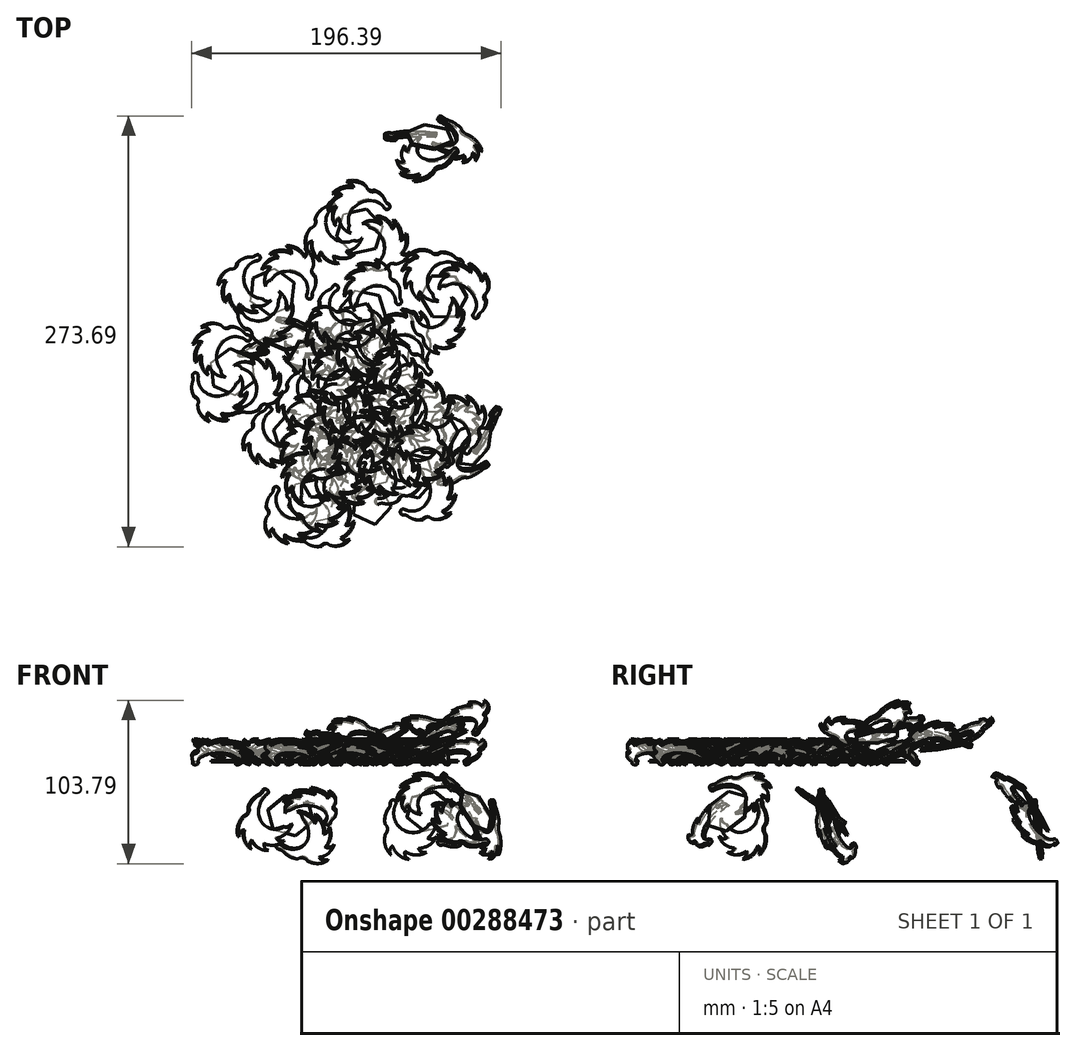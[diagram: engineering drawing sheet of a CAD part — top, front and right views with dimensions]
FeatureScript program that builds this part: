
annotation { "Feature Type Name" : "Feature", "Feature Type Description" : "" }
export const myFeature = defineFeature(function(context is Context, id is Id, definition is map)
    precondition{}
    {
        {
            var Q0;
            Q0=qCreatedBy(makeId("Top.planeOp"),FACE);
            var sketch = newSketch(context, id + "F0", { "sketchPlane" : qUnion([Q0])});
            skCircle(sketch, "E0.cCircle", {"center": v(0, 0) * mm, "radius": 10.32 * mm, "construction": true});
            skLineSegment(sketch, "E0.0", {"start": v(7.5, -10.32) * mm, "end": v(-7.5, -10.32) * mm});
            skLineSegment(sketch, "E0.1", {"start": v(-7.5, -10.32) * mm, "end": v(-12.14, 3.94) * mm});
            skLineSegment(sketch, "E0.2", {"start": v(-12.14, 3.94) * mm, "end": v(0, 12.76) * mm});
            skLineSegment(sketch, "E0.3", {"start": v(0, 12.76) * mm, "end": v(12.14, 3.94) * mm});
            skLineSegment(sketch, "E0.4", {"start": v(12.14, 3.94) * mm, "end": v(7.5, -10.32) * mm});
            skPoint(sketch, "E0.0.midPoint", {"position": v(0, -10.32) * mm});
            skLineSegment(sketch, "E1", {"start": v(0, 12.76) * mm, "end": v(0, -10.32) * mm});
            skSolve(sketch);
        }
        {
            var Q0;
            Q0=qCreatedBy(makeId("Top.planeOp"),FACE);
            var sketch = newSketch(context, id + "F1", { "sketchPlane" : qUnion([Q0])});
            skCircle(sketch, "E2.cCircle", {"center": v(22.17, -7.2) * mm, "radius": 13 * mm, "construction": true});
            skLineSegment(sketch, "E2.0", {"start": v(36.84, -4.09) * mm, "end": v(32.2, -18.35) * mm});
            skLineSegment(sketch, "E2.1", {"start": v(32.2, -18.35) * mm, "end": v(17.54, -21.47) * mm});
            skLineSegment(sketch, "E2.2", {"start": v(17.54, -21.47) * mm, "end": v(7.5, -10.32) * mm});
            skLineSegment(sketch, "E2.3", {"start": v(7.5, -10.32) * mm, "end": v(12.14, 3.94) * mm});
            skLineSegment(sketch, "E2.4", {"start": v(12.14, 3.94) * mm, "end": v(26.8, 7.06) * mm});
            skLineSegment(sketch, "E2.5", {"start": v(26.8, 7.06) * mm, "end": v(36.84, -4.09) * mm});
            skPoint(sketch, "E2.0.midPoint", {"position": v(34.53, -11.22) * mm});
            skSolve(sketch);
        }
        {
            var Q0;
            Q0=makeQuery(id+"F0.imprint","IMPRINT",FACE,{"disambiguationData":[TD([[makeQuery(id+"F0.imprint","IMPRINT",EDGE,{"derivedFrom":sQuery(id+"F0.wireOp",EDGE,"E0.0")}),-1.0]])]});
            extrude(context, id + "F2", {"entities" : qUnion([Q0]), "oppositeDirection" : true, "depth" : 1 * mm});
        }
        {
            var Q0;
            Q0=makeQuery(id+"F1.imprint","IMPRINT",FACE,{"disambiguationData":[TD([[makeQuery(id+"F1.imprint","IMPRINT",EDGE,{"derivedFrom":sQuery(id+"F1.wireOp",EDGE,"E2.0")}),-1.0]])]});
            extrude(context, id + "F3", {"entities" : qUnion([Q0]), "oppositeDirection" : true, "depth" : 1 * mm});
        }
        {
            var Q0;
            Q0=qCreatedBy(makeId("Right.planeOp"),FACE);
            var sketch = newSketch(context, id + "F4", { "sketchPlane" : qUnion([Q0])});
            skLineSegment(sketch, "E3", {"start": v(0, 0) * mm, "end": v(0, 7.73) * mm});
            skSolve(sketch);
        }
        {
            var Q0;
            Q0=makeQuery(id+"F3.opExtrude","SWEPT_BODY",BODY,{"disambiguationData":[OSD([sQuery(id+"F1.wireOp",EDGE,"E2.0"),sQuery(id+"F1.wireOp",EDGE,"E2.1"),sQuery(id+"F1.wireOp",EDGE,"E2.2"),sQuery(id+"F1.wireOp",EDGE,"E2.3"),sQuery(id+"F1.wireOp",EDGE,"E2.4"),sQuery(id+"F1.wireOp",EDGE,"E2.5")])]});
            var Q1;
            Q1=sQuery(id+"F4.wireOp",EDGE,"E3");
            circularPattern(context, id + "F5", {"entities" : qUnion([Q0]), "axis" : qUnion([Q1]), "angle" : 72 * degree, "instanceCount" : round(5)});
        }
        {
            var Q0;
            Q0=makeQuery(id+"F5.opPattern","COPY",FACE,{"derivedFrom":makeQuery(id+"F3.opExtrude","CAP_FACE",FACE,{"disambiguationData":[OSD([sQuery(id+"F1.wireOp",EDGE,"E2.0"),sQuery(id+"F1.wireOp",EDGE,"E2.1"),sQuery(id+"F1.wireOp",EDGE,"E2.2"),sQuery(id+"F1.wireOp",EDGE,"E2.3"),sQuery(id+"F1.wireOp",EDGE,"E2.4"),sQuery(id+"F1.wireOp",EDGE,"E2.5")])],"isStart":true}),"instanceName":"4"});
            var sketch = newSketch(context, id + "F6", { "sketchPlane" : qUnion([Q0])});
            skLineSegment(sketch, "E4", {"start": v(0, -36.3) * mm, "end": v(0, -10.32) * mm});
            skLineSegment(sketch, "E5", {"start": v(-15, -23.31) * mm, "end": v(15, -23.31) * mm});
            skCircle(sketch, "E6", {"center": v(0, -23.31) * mm, "radius": 3.24 * mm});
            skSolve(sketch);
        }
        {
            var Q0;
            Q0=qCreatedBy(makeId("Right.planeOp"),FACE);
            var sketch = newSketch(context, id + "F7", { "sketchPlane" : qUnion([Q0])});
            skArc(sketch, "E7.0", {"start": v(-1.37, 0) * mm, "mid": v(-13.44, 15.63) * mm, "end": v(-25.5, 0) * mm});
            skLineSegment(sketch, "E8", {"start": v(-25.27, 0) * mm, "end": v(-25.5, 0) * mm});
            skLineSegment(sketch, "E9", {"start": v(-1.37, 0) * mm, "end": v(0, 0) * mm});
            skArc(sketch, "E10", {"start": v(1.07, 1.27) * mm, "mid": v(3.46, 7.37) * mm, "end": v(2.5, 13.85) * mm});
            skArc(sketch, "E11", {"start": v(0.8, 19.96) * mm, "mid": v(0.27, 16.52) * mm, "end": v(2.5, 13.85) * mm});
            skArc(sketch, "E12.1.0", {"start": v(0.8, 19.96) * mm, "mid": v(-0.54, 26.93) * mm, "end": v(-5.4, 32.1) * mm});
            skArc(sketch, "E12.1.1", {"start": v(-5.16, 26.31) * mm, "mid": v(-4.13, 29.25) * mm, "end": v(-5.4, 32.1) * mm});
            skArc(sketch, "E12.2.0", {"start": v(-5.16, 26.31) * mm, "mid": v(-10.33, 31.17) * mm, "end": v(-17.3, 32.5) * mm});
            skArc(sketch, "E12.2.1", {"start": v(-13.71, 27.95) * mm, "mid": v(-14.6, 30.93) * mm, "end": v(-17.3, 32.5) * mm});
            skArc(sketch, "E12.3.0", {"start": v(-13.71, 27.95) * mm, "mid": v(-20.75, 28.84) * mm, "end": v(-27.16, 25.82) * mm});
            skArc(sketch, "E12.3.1", {"start": v(-21.6, 24.25) * mm, "mid": v(-24.07, 26.14) * mm, "end": v(-27.16, 25.82) * mm});
            skArc(sketch, "E12.4.0", {"start": v(-21.6, 24.25) * mm, "mid": v(-27.8, 20.83) * mm, "end": v(-31.22, 14.62) * mm});
            skArc(sketch, "E12.4.1", {"start": v(-25.8, 16.63) * mm, "mid": v(-28.9, 16.7) * mm, "end": v(-31.22, 14.62) * mm});
            skArc(sketch, "E12.5.0", {"start": v(-25.8, 16.63) * mm, "mid": v(-28.8, 10.21) * mm, "end": v(-27.92, 3.18) * mm});
            skArc(sketch, "E12.5.1", {"start": v(-24.7, 7.99) * mm, "mid": v(-27.27, 6.22) * mm, "end": v(-27.92, 3.18) * mm});
            skArc(sketch, "E12.6.0", {"start": v(-24.7, 7.99) * mm, "mid": v(-25.75, 4.06) * mm, "end": v(-25.5, 0) * mm});
            skLineSegment(sketch, "E13", {"start": v(-25.5, 0) * mm, "end": v(-25.5, 0) * mm});
            skArc(sketch, "E14", {"start": v(-1.37, 0) * mm, "mid": v(1.27, -2.11) * mm, "end": v(1.07, 1.27) * mm});
            skSolve(sketch);
        }
        {
            var Q0;
            {var subQ2=sQuery(id+"F7.wireOp",EDGE,"E7.0");Q0=makeQuery(id+"F7.imprint","IMPRINT",FACE,{"disambiguationData":[TD([[makeQuery(id+"F7.imprint","IMPRINT",EDGE,{"derivedFrom":subQ2}),-1.0]])]});}
            extrude(context, id + "F8", {"entities" : qUnion([Q0]), "oppositeDirection" : true, "depth" : 2 * mm});
        }
        {
            var Q0;
            Q0=makeQuery(id+"F8.opExtrude","SWEPT_EDGE",EDGE,{"disambiguationData":[OSD([sQuery(id+"F7.wireOp",EDGE,"E10"),sQuery(id+"F7.wireOp",EDGE,"E14")])]});
            fillet(context, id + "F9", {"entities" : qUnion([Q0]), "radius" : 5 * mm, "tangentPropagation" : true, "allowEdgeOverflow" : false});
        }
        {
            var Q0;
            Q0=qCreatedBy(makeId("Right.planeOp"),FACE);
            var sketch = newSketch(context, id + "F10", { "sketchPlane" : qUnion([Q0])});
            skLineSegment(sketch, "E15", {"start": v(0, 0) * mm, "end": v(-23.31, 0) * mm});
            skLineSegment(sketch, "E16", {"start": v(0, 0) * mm, "end": v(0, 28.42) * mm});
            skSolve(sketch);
        }
        {
            var Q0;
            Q0=makeQuery(id+"F8.opExtrude","SWEPT_BODY",BODY,{"disambiguationData":[OSD([sQuery(id+"F7.wireOp",EDGE,"003f2e54-bd62-4f0b-a98e-8c36e71e2cf6"),sQuery(id+"F7.wireOp",EDGE,"8c729305-40a1-49fa-b790-4b99a3909bb6"),sQuery(id+"F7.wireOp",EDGE,"862a2a8f-3db7-4421-9c69-6ab2f53c4c24.1.0"),sQuery(id+"F7.wireOp",EDGE,"862a2a8f-3db7-4421-9c69-6ab2f53c4c24.1.1"),sQuery(id+"F7.wireOp",EDGE,"862a2a8f-3db7-4421-9c69-6ab2f53c4c24.2.0"),sQuery(id+"F7.wireOp",EDGE,"862a2a8f-3db7-4421-9c69-6ab2f53c4c24.2.1"),sQuery(id+"F7.wireOp",EDGE,"862a2a8f-3db7-4421-9c69-6ab2f53c4c24.3.0"),sQuery(id+"F7.wireOp",EDGE,"862a2a8f-3db7-4421-9c69-6ab2f53c4c24.3.1"),sQuery(id+"F7.wireOp",EDGE,"862a2a8f-3db7-4421-9c69-6ab2f53c4c24.4.0"),sQuery(id+"F7.wireOp",EDGE,"862a2a8f-3db7-4421-9c69-6ab2f53c4c24.4.1"),sQuery(id+"F7.wireOp",EDGE,"862a2a8f-3db7-4421-9c69-6ab2f53c4c24.5.0"),sQuery(id+"F7.wireOp",EDGE,"E7.0"),sQuery(id+"F7.wireOp",EDGE,"E8"),sQuery(id+"F7.wireOp",EDGE,"E9")])]});
            var Q1;
            Q1=sQuery(id+"F10.wireOp",EDGE,"E15");
            transform(context, id + "F11", {"entities" : qUnion([Q0]), "transformType" : TransformType.ROTATION, "transformAxis" : qUnion([Q1]), "angle" : 65 * degree, "makeCopy" : false});
        }
        {
            var Q0;
            Q0=makeQuery(id+"F8.opExtrude","SWEPT_BODY",BODY,{"disambiguationData":[OSD([sQuery(id+"F7.wireOp",EDGE,"003f2e54-bd62-4f0b-a98e-8c36e71e2cf6"),sQuery(id+"F7.wireOp",EDGE,"8c729305-40a1-49fa-b790-4b99a3909bb6"),sQuery(id+"F7.wireOp",EDGE,"862a2a8f-3db7-4421-9c69-6ab2f53c4c24.1.0"),sQuery(id+"F7.wireOp",EDGE,"862a2a8f-3db7-4421-9c69-6ab2f53c4c24.1.1"),sQuery(id+"F7.wireOp",EDGE,"862a2a8f-3db7-4421-9c69-6ab2f53c4c24.2.0"),sQuery(id+"F7.wireOp",EDGE,"862a2a8f-3db7-4421-9c69-6ab2f53c4c24.2.1"),sQuery(id+"F7.wireOp",EDGE,"862a2a8f-3db7-4421-9c69-6ab2f53c4c24.3.0"),sQuery(id+"F7.wireOp",EDGE,"862a2a8f-3db7-4421-9c69-6ab2f53c4c24.3.1"),sQuery(id+"F7.wireOp",EDGE,"862a2a8f-3db7-4421-9c69-6ab2f53c4c24.4.0"),sQuery(id+"F7.wireOp",EDGE,"862a2a8f-3db7-4421-9c69-6ab2f53c4c24.4.1"),sQuery(id+"F7.wireOp",EDGE,"862a2a8f-3db7-4421-9c69-6ab2f53c4c24.5.0"),sQuery(id+"F7.wireOp",EDGE,"E7.0"),sQuery(id+"F7.wireOp",EDGE,"E8"),sQuery(id+"F7.wireOp",EDGE,"E9")])]});
            var Q1;
            Q1=sQuery(id+"F10.wireOp",EDGE,"E16");
            circularPattern(context, id + "F12", {"entities" : qUnion([Q0]), "axis" : qUnion([Q1]), "angle" : 72 * degree, "instanceCount" : round(5)});
        }
        {
            var Q0;
            Q0=qCreatedBy(makeId("Right.planeOp"),FACE);
            var sketch = newSketch(context, id + "F13", { "sketchPlane" : qUnion([Q0])});
            skLineSegment(sketch, "E17.0", {"start": v(-36.3, 0) * mm, "end": v(-10.32, 0) * mm});
            skLineSegment(sketch, "E18", {"start": v(-23.31, 0) * mm, "end": v(-23.31, 15.48) * mm});
            skSolve(sketch);
        }
        {
            var Q0;
            Q0=makeQuery(id+"F8.opExtrude","SWEPT_BODY",BODY,{"disambiguationData":[OSD([sQuery(id+"F7.wireOp",EDGE,"003f2e54-bd62-4f0b-a98e-8c36e71e2cf6"),sQuery(id+"F7.wireOp",EDGE,"8c729305-40a1-49fa-b790-4b99a3909bb6"),sQuery(id+"F7.wireOp",EDGE,"862a2a8f-3db7-4421-9c69-6ab2f53c4c24.1.0"),sQuery(id+"F7.wireOp",EDGE,"862a2a8f-3db7-4421-9c69-6ab2f53c4c24.1.1"),sQuery(id+"F7.wireOp",EDGE,"862a2a8f-3db7-4421-9c69-6ab2f53c4c24.2.0"),sQuery(id+"F7.wireOp",EDGE,"862a2a8f-3db7-4421-9c69-6ab2f53c4c24.2.1"),sQuery(id+"F7.wireOp",EDGE,"862a2a8f-3db7-4421-9c69-6ab2f53c4c24.3.0"),sQuery(id+"F7.wireOp",EDGE,"862a2a8f-3db7-4421-9c69-6ab2f53c4c24.3.1"),sQuery(id+"F7.wireOp",EDGE,"862a2a8f-3db7-4421-9c69-6ab2f53c4c24.4.0"),sQuery(id+"F7.wireOp",EDGE,"862a2a8f-3db7-4421-9c69-6ab2f53c4c24.4.1"),sQuery(id+"F7.wireOp",EDGE,"862a2a8f-3db7-4421-9c69-6ab2f53c4c24.5.0"),sQuery(id+"F7.wireOp",EDGE,"E7.0"),sQuery(id+"F7.wireOp",EDGE,"E8"),sQuery(id+"F7.wireOp",EDGE,"E9")])]});
            var Q1;
            Q1=sQuery(id+"F13.wireOp",EDGE,"E18");
            circularPattern(context, id + "F14", {"entities" : qUnion([Q0]), "axis" : qUnion([Q1]), "angle" : 120 * degree, "instanceCount" : round(3)});
        }
        {
            var Q0;
            Q0=makeQuery(id+"F14.opPattern","COPY",BODY,{"derivedFrom":makeQuery(id+"F8.opExtrude","SWEPT_BODY",BODY,{"disambiguationData":[OSD([sQuery(id+"F7.wireOp",EDGE,"E7.0"),sQuery(id+"F7.wireOp",EDGE,"E10"),sQuery(id+"F7.wireOp",EDGE,"E11"),sQuery(id+"F7.wireOp",EDGE,"E12.1.0"),sQuery(id+"F7.wireOp",EDGE,"E12.1.1"),sQuery(id+"F7.wireOp",EDGE,"E12.2.0"),sQuery(id+"F7.wireOp",EDGE,"E12.2.1"),sQuery(id+"F7.wireOp",EDGE,"E12.3.0"),sQuery(id+"F7.wireOp",EDGE,"E12.3.1"),sQuery(id+"F7.wireOp",EDGE,"E12.4.0"),sQuery(id+"F7.wireOp",EDGE,"E12.4.1"),sQuery(id+"F7.wireOp",EDGE,"E12.5.0"),sQuery(id+"F7.wireOp",EDGE,"E12.5.1"),sQuery(id+"F7.wireOp",EDGE,"E12.6.0"),sQuery(id+"F7.wireOp",EDGE,"E13"),sQuery(id+"F7.wireOp",EDGE,"E14")])]}),"instanceName":"2"});
            var Q1;
            Q1=makeQuery(id+"F14.opPattern","COPY",BODY,{"derivedFrom":makeQuery(id+"F8.opExtrude","SWEPT_BODY",BODY,{"disambiguationData":[OSD([sQuery(id+"F7.wireOp",EDGE,"E7.0"),sQuery(id+"F7.wireOp",EDGE,"E10"),sQuery(id+"F7.wireOp",EDGE,"E11"),sQuery(id+"F7.wireOp",EDGE,"E12.1.0"),sQuery(id+"F7.wireOp",EDGE,"E12.1.1"),sQuery(id+"F7.wireOp",EDGE,"E12.2.0"),sQuery(id+"F7.wireOp",EDGE,"E12.2.1"),sQuery(id+"F7.wireOp",EDGE,"E12.3.0"),sQuery(id+"F7.wireOp",EDGE,"E12.3.1"),sQuery(id+"F7.wireOp",EDGE,"E12.4.0"),sQuery(id+"F7.wireOp",EDGE,"E12.4.1"),sQuery(id+"F7.wireOp",EDGE,"E12.5.0"),sQuery(id+"F7.wireOp",EDGE,"E12.5.1"),sQuery(id+"F7.wireOp",EDGE,"E12.6.0"),sQuery(id+"F7.wireOp",EDGE,"E13"),sQuery(id+"F7.wireOp",EDGE,"E14")])]}),"instanceName":"1"});
            var Q2;
            Q2=sQuery(id+"F10.wireOp",EDGE,"E16");
            circularPattern(context, id + "F15", {"entities" : qUnion([Q0, Q1]), "axis" : qUnion([Q2]), "angle" : 72 * degree, "instanceCount" : round(5)});
        }
        {
            var Q0;
            Q0=makeQuery(id+"F3.opExtrude","SWEPT_BODY",BODY,{"disambiguationData":[OSD([sQuery(id+"F1.wireOp",EDGE,"E2.0"),sQuery(id+"F1.wireOp",EDGE,"E2.1"),sQuery(id+"F1.wireOp",EDGE,"E2.2"),sQuery(id+"F1.wireOp",EDGE,"E2.3"),sQuery(id+"F1.wireOp",EDGE,"E2.4"),sQuery(id+"F1.wireOp",EDGE,"E2.5")])]});
            var Q1;
            Q1=makeQuery(id+"F15.opPattern","COPY",BODY,{"derivedFrom":makeQuery(id+"F14.opPattern","COPY",BODY,{"derivedFrom":makeQuery(id+"F8.opExtrude","SWEPT_BODY",BODY,{"disambiguationData":[OSD([sQuery(id+"F7.wireOp",EDGE,"E7.0"),sQuery(id+"F7.wireOp",EDGE,"E10"),sQuery(id+"F7.wireOp",EDGE,"E11"),sQuery(id+"F7.wireOp",EDGE,"E12.1.0"),sQuery(id+"F7.wireOp",EDGE,"E12.1.1"),sQuery(id+"F7.wireOp",EDGE,"E12.2.0"),sQuery(id+"F7.wireOp",EDGE,"E12.2.1"),sQuery(id+"F7.wireOp",EDGE,"E12.3.0"),sQuery(id+"F7.wireOp",EDGE,"E12.3.1"),sQuery(id+"F7.wireOp",EDGE,"E12.4.0"),sQuery(id+"F7.wireOp",EDGE,"E12.4.1"),sQuery(id+"F7.wireOp",EDGE,"E12.5.0"),sQuery(id+"F7.wireOp",EDGE,"E12.5.1"),sQuery(id+"F7.wireOp",EDGE,"E12.6.0"),sQuery(id+"F7.wireOp",EDGE,"E13"),sQuery(id+"F7.wireOp",EDGE,"E14")])]}),"instanceName":"1"}),"instanceName":"1"});
            var Q2;
            Q2=makeQuery(id+"F12.opPattern","COPY",BODY,{"derivedFrom":makeQuery(id+"F8.opExtrude","SWEPT_BODY",BODY,{"disambiguationData":[OSD([sQuery(id+"F7.wireOp",EDGE,"E7.0"),sQuery(id+"F7.wireOp",EDGE,"E10"),sQuery(id+"F7.wireOp",EDGE,"E11"),sQuery(id+"F7.wireOp",EDGE,"E12.1.0"),sQuery(id+"F7.wireOp",EDGE,"E12.1.1"),sQuery(id+"F7.wireOp",EDGE,"E12.2.0"),sQuery(id+"F7.wireOp",EDGE,"E12.2.1"),sQuery(id+"F7.wireOp",EDGE,"E12.3.0"),sQuery(id+"F7.wireOp",EDGE,"E12.3.1"),sQuery(id+"F7.wireOp",EDGE,"E12.4.0"),sQuery(id+"F7.wireOp",EDGE,"E12.4.1"),sQuery(id+"F7.wireOp",EDGE,"E12.5.0"),sQuery(id+"F7.wireOp",EDGE,"E12.5.1"),sQuery(id+"F7.wireOp",EDGE,"E12.6.0"),sQuery(id+"F7.wireOp",EDGE,"E13"),sQuery(id+"F7.wireOp",EDGE,"E14")])]}),"instanceName":"1"});
            var Q3;
            Q3=makeQuery(id+"F15.opPattern","COPY",BODY,{"derivedFrom":makeQuery(id+"F14.opPattern","COPY",BODY,{"derivedFrom":makeQuery(id+"F8.opExtrude","SWEPT_BODY",BODY,{"disambiguationData":[OSD([sQuery(id+"F7.wireOp",EDGE,"E7.0"),sQuery(id+"F7.wireOp",EDGE,"E10"),sQuery(id+"F7.wireOp",EDGE,"E11"),sQuery(id+"F7.wireOp",EDGE,"E12.1.0"),sQuery(id+"F7.wireOp",EDGE,"E12.1.1"),sQuery(id+"F7.wireOp",EDGE,"E12.2.0"),sQuery(id+"F7.wireOp",EDGE,"E12.2.1"),sQuery(id+"F7.wireOp",EDGE,"E12.3.0"),sQuery(id+"F7.wireOp",EDGE,"E12.3.1"),sQuery(id+"F7.wireOp",EDGE,"E12.4.0"),sQuery(id+"F7.wireOp",EDGE,"E12.4.1"),sQuery(id+"F7.wireOp",EDGE,"E12.5.0"),sQuery(id+"F7.wireOp",EDGE,"E12.5.1"),sQuery(id+"F7.wireOp",EDGE,"E12.6.0"),sQuery(id+"F7.wireOp",EDGE,"E13"),sQuery(id+"F7.wireOp",EDGE,"E14")])]}),"instanceName":"2"}),"instanceName":"1"});
            var Q4;
            Q4=sQuery(id+"F13.wireOp",EDGE,"E18");
            circularPattern(context, id + "F16", {"entities" : qUnion([Q0, Q1, Q2, Q3]), "axis" : qUnion([Q4]), "angle" : 120 * degree, "instanceCount" : 2, "oppositeDirection" : true});
        }
        {
            var Q0;
            Q0=makeQuery(id+"F2.opExtrude","SWEPT_BODY",BODY,{"disambiguationData":[OSD([sQuery(id+"F0.wireOp",EDGE,"E0.0"),sQuery(id+"F0.wireOp",EDGE,"E0.1"),sQuery(id+"F0.wireOp",EDGE,"E0.2"),sQuery(id+"F0.wireOp",EDGE,"E0.3"),sQuery(id+"F0.wireOp",EDGE,"E0.4")])]});
            var Q1;
            Q1=makeQuery(id+"F12.opPattern","COPY",BODY,{"derivedFrom":makeQuery(id+"F8.opExtrude","SWEPT_BODY",BODY,{"disambiguationData":[OSD([sQuery(id+"F7.wireOp",EDGE,"E7.0"),sQuery(id+"F7.wireOp",EDGE,"E10"),sQuery(id+"F7.wireOp",EDGE,"E11"),sQuery(id+"F7.wireOp",EDGE,"E12.1.0"),sQuery(id+"F7.wireOp",EDGE,"E12.1.1"),sQuery(id+"F7.wireOp",EDGE,"E12.2.0"),sQuery(id+"F7.wireOp",EDGE,"E12.2.1"),sQuery(id+"F7.wireOp",EDGE,"E12.3.0"),sQuery(id+"F7.wireOp",EDGE,"E12.3.1"),sQuery(id+"F7.wireOp",EDGE,"E12.4.0"),sQuery(id+"F7.wireOp",EDGE,"E12.4.1"),sQuery(id+"F7.wireOp",EDGE,"E12.5.0"),sQuery(id+"F7.wireOp",EDGE,"E12.5.1"),sQuery(id+"F7.wireOp",EDGE,"E12.6.0"),sQuery(id+"F7.wireOp",EDGE,"E13"),sQuery(id+"F7.wireOp",EDGE,"E14")])]}),"instanceName":"2"});
            var Q2;
            Q2=makeQuery(id+"F12.opPattern","COPY",BODY,{"derivedFrom":makeQuery(id+"F8.opExtrude","SWEPT_BODY",BODY,{"disambiguationData":[OSD([sQuery(id+"F7.wireOp",EDGE,"E7.0"),sQuery(id+"F7.wireOp",EDGE,"E10"),sQuery(id+"F7.wireOp",EDGE,"E11"),sQuery(id+"F7.wireOp",EDGE,"E12.1.0"),sQuery(id+"F7.wireOp",EDGE,"E12.1.1"),sQuery(id+"F7.wireOp",EDGE,"E12.2.0"),sQuery(id+"F7.wireOp",EDGE,"E12.2.1"),sQuery(id+"F7.wireOp",EDGE,"E12.3.0"),sQuery(id+"F7.wireOp",EDGE,"E12.3.1"),sQuery(id+"F7.wireOp",EDGE,"E12.4.0"),sQuery(id+"F7.wireOp",EDGE,"E12.4.1"),sQuery(id+"F7.wireOp",EDGE,"E12.5.0"),sQuery(id+"F7.wireOp",EDGE,"E12.5.1"),sQuery(id+"F7.wireOp",EDGE,"E12.6.0"),sQuery(id+"F7.wireOp",EDGE,"E13"),sQuery(id+"F7.wireOp",EDGE,"E14")])]}),"instanceName":"3"});
            var Q3;
            Q3=sQuery(id+"F13.wireOp",EDGE,"E18");
            circularPattern(context, id + "F17", {"entities" : qUnion([Q0, Q1, Q2]), "axis" : qUnion([Q3]), "angle" : 120 * degree, "instanceCount" : round(3)});
        }
        {
            var Q0;
            Q0=makeQuery(id+"F17.opPattern","COPY",FACE,{"derivedFrom":makeQuery(id+"F2.opExtrude","CAP_FACE",FACE,{"disambiguationData":[OSD([sQuery(id+"F0.wireOp",EDGE,"E0.0"),sQuery(id+"F0.wireOp",EDGE,"E0.1"),sQuery(id+"F0.wireOp",EDGE,"E0.2"),sQuery(id+"F0.wireOp",EDGE,"E0.3"),sQuery(id+"F0.wireOp",EDGE,"E0.4")])],"isStart":true}),"instanceName":"1"});
            var sketch = newSketch(context, id + "F18", { "sketchPlane" : qUnion([Q0])});
            skLineSegment(sketch, "E19", {"start": v(-11.25, -29.8) * mm, "end": v(-31.24, -41.35) * mm});
            skLineSegment(sketch, "E20", {"start": v(-19.97, -22.2) * mm, "end": v(-12.52, -41.88) * mm});
            skSolve(sketch);
        }
        {
            var Q0;
            Q0=sQuery(id+"F18.wireOp",VERTEX,"E19.end");
            var Q1;
            Q1=sQuery(id+"F18.wireOp",VERTEX,"E19.start");
            var Q2;
            Q2=sQuery(id+"F13.wireOp",VERTEX,"E18.end");
            cPlane(context, id + "F19", {"entities" : qUnion([Q0, Q1, Q2]), "cplaneType" : CPlaneType.THREE_POINT, "offset" : 150 * mm, "width" : 150 * mm, "height" : 150 * mm});
        }
        {
            var Q0;
            Q0=qCreatedBy(id+"F19.planeOp",FACE);
            var sketch = newSketch(context, id + "F20", { "sketchPlane" : qUnion([Q0])});
            skLineSegment(sketch, "E21.0", {"start": v(24.65, 0) * mm, "end": v(47.73, 0) * mm});
            skLineSegment(sketch, "E21.1", {"start": v(28.4, 0) * mm, "end": v(31.78, 0) * mm});
            skLineSegment(sketch, "E22", {"start": v(31.8, 0) * mm, "end": v(31.8, 2.35) * mm});
            skLineSegment(sketch, "E23", {"start": v(31.8, 2.35) * mm, "end": v(31.8, 9.54) * mm});
            skSolve(sketch);
        }
        {
            var Q0;
            Q0=makeQuery(id+"F16.opPattern","COPY",BODY,{"derivedFrom":makeQuery(id+"F3.opExtrude","SWEPT_BODY",BODY,{"disambiguationData":[OSD([sQuery(id+"F1.wireOp",EDGE,"E2.0"),sQuery(id+"F1.wireOp",EDGE,"E2.1"),sQuery(id+"F1.wireOp",EDGE,"E2.2"),sQuery(id+"F1.wireOp",EDGE,"E2.3"),sQuery(id+"F1.wireOp",EDGE,"E2.4"),sQuery(id+"F1.wireOp",EDGE,"E2.5")])]}),"instanceName":"1"});
            var Q1;
            Q1=makeQuery(id+"F16.opPattern","COPY",BODY,{"derivedFrom":makeQuery(id+"F12.opPattern","COPY",BODY,{"derivedFrom":makeQuery(id+"F8.opExtrude","SWEPT_BODY",BODY,{"disambiguationData":[OSD([sQuery(id+"F7.wireOp",EDGE,"E7.0"),sQuery(id+"F7.wireOp",EDGE,"E10"),sQuery(id+"F7.wireOp",EDGE,"E11"),sQuery(id+"F7.wireOp",EDGE,"E12.1.0"),sQuery(id+"F7.wireOp",EDGE,"E12.1.1"),sQuery(id+"F7.wireOp",EDGE,"E12.2.0"),sQuery(id+"F7.wireOp",EDGE,"E12.2.1"),sQuery(id+"F7.wireOp",EDGE,"E12.3.0"),sQuery(id+"F7.wireOp",EDGE,"E12.3.1"),sQuery(id+"F7.wireOp",EDGE,"E12.4.0"),sQuery(id+"F7.wireOp",EDGE,"E12.4.1"),sQuery(id+"F7.wireOp",EDGE,"E12.5.0"),sQuery(id+"F7.wireOp",EDGE,"E12.5.1"),sQuery(id+"F7.wireOp",EDGE,"E12.6.0"),sQuery(id+"F7.wireOp",EDGE,"E13"),sQuery(id+"F7.wireOp",EDGE,"E14")])]}),"instanceName":"1"}),"instanceName":"1"});
            var Q2;
            Q2=makeQuery(id+"F16.opPattern","COPY",BODY,{"derivedFrom":makeQuery(id+"F15.opPattern","COPY",BODY,{"derivedFrom":makeQuery(id+"F14.opPattern","COPY",BODY,{"derivedFrom":makeQuery(id+"F8.opExtrude","SWEPT_BODY",BODY,{"disambiguationData":[OSD([sQuery(id+"F7.wireOp",EDGE,"E7.0"),sQuery(id+"F7.wireOp",EDGE,"E10"),sQuery(id+"F7.wireOp",EDGE,"E11"),sQuery(id+"F7.wireOp",EDGE,"E12.1.0"),sQuery(id+"F7.wireOp",EDGE,"E12.1.1"),sQuery(id+"F7.wireOp",EDGE,"E12.2.0"),sQuery(id+"F7.wireOp",EDGE,"E12.2.1"),sQuery(id+"F7.wireOp",EDGE,"E12.3.0"),sQuery(id+"F7.wireOp",EDGE,"E12.3.1"),sQuery(id+"F7.wireOp",EDGE,"E12.4.0"),sQuery(id+"F7.wireOp",EDGE,"E12.4.1"),sQuery(id+"F7.wireOp",EDGE,"E12.5.0"),sQuery(id+"F7.wireOp",EDGE,"E12.5.1"),sQuery(id+"F7.wireOp",EDGE,"E12.6.0"),sQuery(id+"F7.wireOp",EDGE,"E13"),sQuery(id+"F7.wireOp",EDGE,"E14")])]}),"instanceName":"2"}),"instanceName":"1"}),"instanceName":"1"});
            var Q3;
            Q3=makeQuery(id+"F16.opPattern","COPY",BODY,{"derivedFrom":makeQuery(id+"F15.opPattern","COPY",BODY,{"derivedFrom":makeQuery(id+"F14.opPattern","COPY",BODY,{"derivedFrom":makeQuery(id+"F8.opExtrude","SWEPT_BODY",BODY,{"disambiguationData":[OSD([sQuery(id+"F7.wireOp",EDGE,"E7.0"),sQuery(id+"F7.wireOp",EDGE,"E10"),sQuery(id+"F7.wireOp",EDGE,"E11"),sQuery(id+"F7.wireOp",EDGE,"E12.1.0"),sQuery(id+"F7.wireOp",EDGE,"E12.1.1"),sQuery(id+"F7.wireOp",EDGE,"E12.2.0"),sQuery(id+"F7.wireOp",EDGE,"E12.2.1"),sQuery(id+"F7.wireOp",EDGE,"E12.3.0"),sQuery(id+"F7.wireOp",EDGE,"E12.3.1"),sQuery(id+"F7.wireOp",EDGE,"E12.4.0"),sQuery(id+"F7.wireOp",EDGE,"E12.4.1"),sQuery(id+"F7.wireOp",EDGE,"E12.5.0"),sQuery(id+"F7.wireOp",EDGE,"E12.5.1"),sQuery(id+"F7.wireOp",EDGE,"E12.6.0"),sQuery(id+"F7.wireOp",EDGE,"E13"),sQuery(id+"F7.wireOp",EDGE,"E14")])]}),"instanceName":"1"}),"instanceName":"1"}),"instanceName":"1"});
            var Q4;
            Q4=sQuery(id+"F20.wireOp",EDGE,"E22");
            circularPattern(context, id + "F21", {"entities" : qUnion([Q0, Q1, Q2, Q3]), "axis" : qUnion([Q4]), "angle" : 72 * degree, "instanceCount" : round(3), "oppositeDirection" : true});
        }
        {
            var Q0;
            Q0=makeQuery(id+"F17.opPattern","COPY",FACE,{"derivedFrom":makeQuery(id+"F2.opExtrude","CAP_FACE",FACE,{"disambiguationData":[OSD([sQuery(id+"F0.wireOp",EDGE,"E0.0"),sQuery(id+"F0.wireOp",EDGE,"E0.1"),sQuery(id+"F0.wireOp",EDGE,"E0.2"),sQuery(id+"F0.wireOp",EDGE,"E0.3"),sQuery(id+"F0.wireOp",EDGE,"E0.4")])],"isStart":true}),"instanceName":"2"});
            var sketch = newSketch(context, id + "F22", { "sketchPlane" : qUnion([Q0])});
            skLineSegment(sketch, "E24", {"start": v(11.25, -29.8) * mm, "end": v(31.24, -41.35) * mm});
            skLineSegment(sketch, "E25", {"start": v(17.54, -47.45) * mm, "end": v(22.34, -24.87) * mm});
            skSolve(sketch);
        }
        {
            var Q0;
            Q0=sQuery(id+"F22.wireOp",VERTEX,"E24.end");
            var Q1;
            Q1=sQuery(id+"F22.wireOp",VERTEX,"E24.start");
            var Q2;
            Q2=sQuery(id+"F13.wireOp",VERTEX,"E18.end");
            cPlane(context, id + "F23", {"entities" : qUnion([Q0, Q1, Q2]), "cplaneType" : CPlaneType.THREE_POINT, "offset" : 150 * mm, "width" : 150 * mm, "height" : 150 * mm});
        }
        {
            var Q0;
            Q0=qCreatedBy(id+"F23.planeOp",FACE);
            var sketch = newSketch(context, id + "F24", { "sketchPlane" : qUnion([Q0])});
            skLineSegment(sketch, "E26.0", {"start": v(24.65, 0) * mm, "end": v(47.73, 0) * mm});
            skLineSegment(sketch, "E26.1", {"start": v(38.91, 0) * mm, "end": v(31.78, 0) * mm});
            skLineSegment(sketch, "E27", {"start": v(31.8, 0) * mm, "end": v(31.8, 7.31) * mm});
            skSolve(sketch);
        }
        {
            var Q0;
            Q0=makeQuery(id+"F3.opExtrude","SWEPT_BODY",BODY,{"disambiguationData":[OSD([sQuery(id+"F1.wireOp",EDGE,"E2.0"),sQuery(id+"F1.wireOp",EDGE,"E2.1"),sQuery(id+"F1.wireOp",EDGE,"E2.2"),sQuery(id+"F1.wireOp",EDGE,"E2.3"),sQuery(id+"F1.wireOp",EDGE,"E2.4"),sQuery(id+"F1.wireOp",EDGE,"E2.5")])]});
            var Q1;
            Q1=makeQuery(id+"F15.opPattern","COPY",BODY,{"derivedFrom":makeQuery(id+"F14.opPattern","COPY",BODY,{"derivedFrom":makeQuery(id+"F8.opExtrude","SWEPT_BODY",BODY,{"disambiguationData":[OSD([sQuery(id+"F7.wireOp",EDGE,"E7.0"),sQuery(id+"F7.wireOp",EDGE,"E10"),sQuery(id+"F7.wireOp",EDGE,"E11"),sQuery(id+"F7.wireOp",EDGE,"E12.1.0"),sQuery(id+"F7.wireOp",EDGE,"E12.1.1"),sQuery(id+"F7.wireOp",EDGE,"E12.2.0"),sQuery(id+"F7.wireOp",EDGE,"E12.2.1"),sQuery(id+"F7.wireOp",EDGE,"E12.3.0"),sQuery(id+"F7.wireOp",EDGE,"E12.3.1"),sQuery(id+"F7.wireOp",EDGE,"E12.4.0"),sQuery(id+"F7.wireOp",EDGE,"E12.4.1"),sQuery(id+"F7.wireOp",EDGE,"E12.5.0"),sQuery(id+"F7.wireOp",EDGE,"E12.5.1"),sQuery(id+"F7.wireOp",EDGE,"E12.6.0"),sQuery(id+"F7.wireOp",EDGE,"E13"),sQuery(id+"F7.wireOp",EDGE,"E14")])]}),"instanceName":"2"}),"instanceName":"1"});
            var Q2;
            Q2=makeQuery(id+"F12.opPattern","COPY",BODY,{"derivedFrom":makeQuery(id+"F8.opExtrude","SWEPT_BODY",BODY,{"disambiguationData":[OSD([sQuery(id+"F7.wireOp",EDGE,"E7.0"),sQuery(id+"F7.wireOp",EDGE,"E10"),sQuery(id+"F7.wireOp",EDGE,"E11"),sQuery(id+"F7.wireOp",EDGE,"E12.1.0"),sQuery(id+"F7.wireOp",EDGE,"E12.1.1"),sQuery(id+"F7.wireOp",EDGE,"E12.2.0"),sQuery(id+"F7.wireOp",EDGE,"E12.2.1"),sQuery(id+"F7.wireOp",EDGE,"E12.3.0"),sQuery(id+"F7.wireOp",EDGE,"E12.3.1"),sQuery(id+"F7.wireOp",EDGE,"E12.4.0"),sQuery(id+"F7.wireOp",EDGE,"E12.4.1"),sQuery(id+"F7.wireOp",EDGE,"E12.5.0"),sQuery(id+"F7.wireOp",EDGE,"E12.5.1"),sQuery(id+"F7.wireOp",EDGE,"E12.6.0"),sQuery(id+"F7.wireOp",EDGE,"E13"),sQuery(id+"F7.wireOp",EDGE,"E14")])]}),"instanceName":"1"});
            var Q3;
            Q3=makeQuery(id+"F15.opPattern","COPY",BODY,{"derivedFrom":makeQuery(id+"F14.opPattern","COPY",BODY,{"derivedFrom":makeQuery(id+"F8.opExtrude","SWEPT_BODY",BODY,{"disambiguationData":[OSD([sQuery(id+"F7.wireOp",EDGE,"E7.0"),sQuery(id+"F7.wireOp",EDGE,"E10"),sQuery(id+"F7.wireOp",EDGE,"E11"),sQuery(id+"F7.wireOp",EDGE,"E12.1.0"),sQuery(id+"F7.wireOp",EDGE,"E12.1.1"),sQuery(id+"F7.wireOp",EDGE,"E12.2.0"),sQuery(id+"F7.wireOp",EDGE,"E12.2.1"),sQuery(id+"F7.wireOp",EDGE,"E12.3.0"),sQuery(id+"F7.wireOp",EDGE,"E12.3.1"),sQuery(id+"F7.wireOp",EDGE,"E12.4.0"),sQuery(id+"F7.wireOp",EDGE,"E12.4.1"),sQuery(id+"F7.wireOp",EDGE,"E12.5.0"),sQuery(id+"F7.wireOp",EDGE,"E12.5.1"),sQuery(id+"F7.wireOp",EDGE,"E12.6.0"),sQuery(id+"F7.wireOp",EDGE,"E13"),sQuery(id+"F7.wireOp",EDGE,"E14")])]}),"instanceName":"1"}),"instanceName":"1"});
            var Q4;
            Q4=sQuery(id+"F24.wireOp",EDGE,"E27");
            circularPattern(context, id + "F25", {"entities" : qUnion([Q0, Q1, Q2, Q3]), "axis" : qUnion([Q4]), "angle" : 72 * degree, "instanceCount" : round(3), "oppositeDirection" : true});
        }
        {
            var Q0;
            Q0=makeQuery(id+"F16.opPattern","COPY",FACE,{"derivedFrom":makeQuery(id+"F3.opExtrude","CAP_FACE",FACE,{"disambiguationData":[OSD([sQuery(id+"F1.wireOp",EDGE,"E2.0"),sQuery(id+"F1.wireOp",EDGE,"E2.1"),sQuery(id+"F1.wireOp",EDGE,"E2.2"),sQuery(id+"F1.wireOp",EDGE,"E2.3"),sQuery(id+"F1.wireOp",EDGE,"E2.4"),sQuery(id+"F1.wireOp",EDGE,"E2.5")])],"isStart":true}),"instanceName":"1"});
            var sketch = newSketch(context, id + "F26", { "sketchPlane" : qUnion([Q0])});
            skLineSegment(sketch, "E28", {"start": v(5.57, -63.28) * mm, "end": v(0.16, -37.86) * mm});
            skSolve(sketch);
        }
        {
            var Q0;
            Q0=qCreatedBy(makeId("Right.planeOp"),FACE);
            var sketch = newSketch(context, id + "F27", { "sketchPlane" : qUnion([Q0])});
            skLineSegment(sketch, "E29.0", {"start": v(-63.28, 0) * mm, "end": v(-37.86, 0) * mm});
            skLineSegment(sketch, "E30", {"start": v(-50.57, 0) * mm, "end": v(-50.57, 14.45) * mm});
            skSolve(sketch);
        }
        {
            var Q0;
            Q0=makeQuery(id+"F17.opPattern","COPY",BODY,{"derivedFrom":makeQuery(id+"F2.opExtrude","SWEPT_BODY",BODY,{"disambiguationData":[OSD([sQuery(id+"F0.wireOp",EDGE,"E0.0"),sQuery(id+"F0.wireOp",EDGE,"E0.1"),sQuery(id+"F0.wireOp",EDGE,"E0.2"),sQuery(id+"F0.wireOp",EDGE,"E0.3"),sQuery(id+"F0.wireOp",EDGE,"E0.4")])]}),"instanceName":"2"});
            var Q1;
            Q1=sQuery(id+"F27.wireOp",EDGE,"E30");
            circularPattern(context, id + "F28", {"entities" : qUnion([Q0]), "axis" : qUnion([Q1]), "angle" : 120 * degree, "instanceCount" : 2, "oppositeDirection" : true});
        }
        {
            var Q0;
            Q0=makeQuery(id+"F28.opPattern","COPY",FACE,{"derivedFrom":makeQuery(id+"F17.opPattern","COPY",FACE,{"derivedFrom":makeQuery(id+"F2.opExtrude","CAP_FACE",FACE,{"disambiguationData":[OSD([sQuery(id+"F0.wireOp",EDGE,"E0.0"),sQuery(id+"F0.wireOp",EDGE,"E0.1"),sQuery(id+"F0.wireOp",EDGE,"E0.2"),sQuery(id+"F0.wireOp",EDGE,"E0.3"),sQuery(id+"F0.wireOp",EDGE,"E0.4")])],"isStart":true}),"instanceName":"2"}),"instanceName":"1"});
            var sketch = newSketch(context, id + "F29", { "sketchPlane" : qUnion([Q0])});
            skLineSegment(sketch, "E31", {"start": v(6.07, -88.34) * mm, "end": v(3.41, -75.85) * mm});
            skLineSegment(sketch, "E32", {"start": v(-7.64, -82.23) * mm, "end": v(12.35, -70.7) * mm});
            skPoint(sketch, "E33.orphan", {"position": v(1.27, -65.76) * mm});
            skSolve(sketch);
        }
        {
            var Q0;
            Q0=qCreatedBy(makeId("Right.planeOp"),FACE);
            var sketch = newSketch(context, id + "F30", { "sketchPlane" : qUnion([Q0])});
            skLineSegment(sketch, "E34.0", {"start": v(-88.34, 0) * mm, "end": v(-75.85, 0) * mm});
            skLineSegment(sketch, "E35", {"start": v(-75.85, 0) * mm, "end": v(-75.85, -22.18) * mm});
            skSolve(sketch);
        }
        {
            var Q0;
            Q0=makeQuery(id+"F25.opPattern","COPY",BODY,{"derivedFrom":makeQuery(id+"F3.opExtrude","SWEPT_BODY",BODY,{"disambiguationData":[OSD([sQuery(id+"F1.wireOp",EDGE,"E2.0"),sQuery(id+"F1.wireOp",EDGE,"E2.1"),sQuery(id+"F1.wireOp",EDGE,"E2.2"),sQuery(id+"F1.wireOp",EDGE,"E2.3"),sQuery(id+"F1.wireOp",EDGE,"E2.4"),sQuery(id+"F1.wireOp",EDGE,"E2.5")])]}),"instanceName":"2"});
            var Q1;
            Q1=makeQuery(id+"F25.opPattern","COPY",BODY,{"derivedFrom":makeQuery(id+"F15.opPattern","COPY",BODY,{"derivedFrom":makeQuery(id+"F14.opPattern","COPY",BODY,{"derivedFrom":makeQuery(id+"F8.opExtrude","SWEPT_BODY",BODY,{"disambiguationData":[OSD([sQuery(id+"F7.wireOp",EDGE,"E7.0"),sQuery(id+"F7.wireOp",EDGE,"E10"),sQuery(id+"F7.wireOp",EDGE,"E11"),sQuery(id+"F7.wireOp",EDGE,"E12.1.0"),sQuery(id+"F7.wireOp",EDGE,"E12.1.1"),sQuery(id+"F7.wireOp",EDGE,"E12.2.0"),sQuery(id+"F7.wireOp",EDGE,"E12.2.1"),sQuery(id+"F7.wireOp",EDGE,"E12.3.0"),sQuery(id+"F7.wireOp",EDGE,"E12.3.1"),sQuery(id+"F7.wireOp",EDGE,"E12.4.0"),sQuery(id+"F7.wireOp",EDGE,"E12.4.1"),sQuery(id+"F7.wireOp",EDGE,"E12.5.0"),sQuery(id+"F7.wireOp",EDGE,"E12.5.1"),sQuery(id+"F7.wireOp",EDGE,"E12.6.0"),sQuery(id+"F7.wireOp",EDGE,"E13"),sQuery(id+"F7.wireOp",EDGE,"E14")])]}),"instanceName":"2"}),"instanceName":"1"}),"instanceName":"2"});
            var Q2;
            Q2=makeQuery(id+"F25.opPattern","COPY",BODY,{"derivedFrom":makeQuery(id+"F12.opPattern","COPY",BODY,{"derivedFrom":makeQuery(id+"F8.opExtrude","SWEPT_BODY",BODY,{"disambiguationData":[OSD([sQuery(id+"F7.wireOp",EDGE,"E7.0"),sQuery(id+"F7.wireOp",EDGE,"E10"),sQuery(id+"F7.wireOp",EDGE,"E11"),sQuery(id+"F7.wireOp",EDGE,"E12.1.0"),sQuery(id+"F7.wireOp",EDGE,"E12.1.1"),sQuery(id+"F7.wireOp",EDGE,"E12.2.0"),sQuery(id+"F7.wireOp",EDGE,"E12.2.1"),sQuery(id+"F7.wireOp",EDGE,"E12.3.0"),sQuery(id+"F7.wireOp",EDGE,"E12.3.1"),sQuery(id+"F7.wireOp",EDGE,"E12.4.0"),sQuery(id+"F7.wireOp",EDGE,"E12.4.1"),sQuery(id+"F7.wireOp",EDGE,"E12.5.0"),sQuery(id+"F7.wireOp",EDGE,"E12.5.1"),sQuery(id+"F7.wireOp",EDGE,"E12.6.0"),sQuery(id+"F7.wireOp",EDGE,"E13"),sQuery(id+"F7.wireOp",EDGE,"E14")])]}),"instanceName":"1"}),"instanceName":"2"});
            var Q3;
            Q3=makeQuery(id+"F17.opPattern","COPY",BODY,{"derivedFrom":makeQuery(id+"F12.opPattern","COPY",BODY,{"derivedFrom":makeQuery(id+"F8.opExtrude","SWEPT_BODY",BODY,{"disambiguationData":[OSD([sQuery(id+"F7.wireOp",EDGE,"E7.0"),sQuery(id+"F7.wireOp",EDGE,"E10"),sQuery(id+"F7.wireOp",EDGE,"E11"),sQuery(id+"F7.wireOp",EDGE,"E12.1.0"),sQuery(id+"F7.wireOp",EDGE,"E12.1.1"),sQuery(id+"F7.wireOp",EDGE,"E12.2.0"),sQuery(id+"F7.wireOp",EDGE,"E12.2.1"),sQuery(id+"F7.wireOp",EDGE,"E12.3.0"),sQuery(id+"F7.wireOp",EDGE,"E12.3.1"),sQuery(id+"F7.wireOp",EDGE,"E12.4.0"),sQuery(id+"F7.wireOp",EDGE,"E12.4.1"),sQuery(id+"F7.wireOp",EDGE,"E12.5.0"),sQuery(id+"F7.wireOp",EDGE,"E12.5.1"),sQuery(id+"F7.wireOp",EDGE,"E12.6.0"),sQuery(id+"F7.wireOp",EDGE,"E13"),sQuery(id+"F7.wireOp",EDGE,"E14")])]}),"instanceName":"2"}),"instanceName":"2"});
            var Q4;
            Q4=sQuery(id+"F30.wireOp",EDGE,"E35");
            circularPattern(context, id + "F31", {"entities" : qUnion([Q0, Q1, Q2, Q3]), "axis" : qUnion([Q4]), "angle" : 72 * degree, "instanceCount" : round(3), "oppositeDirection" : true});
        }
        {
            var Q0;
            Q0=makeQuery(id+"F5.opPattern","COPY",FACE,{"derivedFrom":makeQuery(id+"F3.opExtrude","CAP_FACE",FACE,{"disambiguationData":[OSD([sQuery(id+"F1.wireOp",EDGE,"E2.0"),sQuery(id+"F1.wireOp",EDGE,"E2.1"),sQuery(id+"F1.wireOp",EDGE,"E2.2"),sQuery(id+"F1.wireOp",EDGE,"E2.3"),sQuery(id+"F1.wireOp",EDGE,"E2.4"),sQuery(id+"F1.wireOp",EDGE,"E2.5")])],"isStart":true}),"instanceName":"2"});
            var sketch = newSketch(context, id + "F32", { "sketchPlane" : qUnion([Q0])});
            skLineSegment(sketch, "E36", {"start": v(-6.07, 8.35) * mm, "end": v(-21.34, 29.37) * mm});
            skSolve(sketch);
        }
        {
            var Q0;
            Q0=sQuery(id+"F32.wireOp",VERTEX,"E36.end");
            var Q1;
            Q1=sQuery(id+"F32.wireOp",VERTEX,"E36.start");
            var Q2;
            Q2=sQuery(id+"F10.wireOp",VERTEX,"E16.end");
            cPlane(context, id + "F33", {"entities" : qUnion([Q0, Q1, Q2]), "cplaneType" : CPlaneType.THREE_POINT, "offset" : 150 * mm, "width" : 150 * mm, "height" : 150 * mm});
        }
        {
            var Q0;
            Q0=qCreatedBy(id+"F33.planeOp",FACE);
            var sketch = newSketch(context, id + "F34", { "sketchPlane" : qUnion([Q0])});
            skLineSegment(sketch, "E37.0", {"start": v(10.32, 0) * mm, "end": v(36.3, 0) * mm});
            skLineSegment(sketch, "E38", {"start": v(23.31, 0) * mm, "end": v(23.31, 29.53) * mm});
            skSolve(sketch);
        }
        {
            var Q0;
            Q0=makeQuery(id+"F2.opExtrude","SWEPT_BODY",BODY,{"disambiguationData":[OSD([sQuery(id+"F0.wireOp",EDGE,"E0.0"),sQuery(id+"F0.wireOp",EDGE,"E0.1"),sQuery(id+"F0.wireOp",EDGE,"E0.2"),sQuery(id+"F0.wireOp",EDGE,"E0.3"),sQuery(id+"F0.wireOp",EDGE,"E0.4")])]});
            var Q1;
            Q1=sQuery(id+"F34.wireOp",EDGE,"E38");
            circularPattern(context, id + "F35", {"entities" : qUnion([Q0]), "axis" : qUnion([Q1]), "angle" : 120 * degree, "instanceCount" : round(3), "oppositeDirection" : true});
        }
        {
            var Q0;
            Q0=makeQuery(id+"F35.opPattern","COPY",FACE,{"derivedFrom":makeQuery(id+"F2.opExtrude","CAP_FACE",FACE,{"disambiguationData":[OSD([sQuery(id+"F0.wireOp",EDGE,"E0.0"),sQuery(id+"F0.wireOp",EDGE,"E0.1"),sQuery(id+"F0.wireOp",EDGE,"E0.2"),sQuery(id+"F0.wireOp",EDGE,"E0.3"),sQuery(id+"F0.wireOp",EDGE,"E0.4")])],"isStart":true}),"instanceName":"1"});
            var sketch = newSketch(context, id + "F36", { "sketchPlane" : qUnion([Q0])});
            skLineSegment(sketch, "E39", {"start": v(-36.89, 16.42) * mm, "end": v(-49.58, 15.1) * mm});
            skPoint(sketch, "E40.orphan", {"position": v(-26.62, 17.5) * mm});
            skSolve(sketch);
        }
        {
            var Q0;
            Q0=sQuery(id+"F36.wireOp",VERTEX,"E39.end");
            var Q1;
            Q1=sQuery(id+"F36.wireOp",VERTEX,"E39.start");
            var Q2;
            Q2=sQuery(id+"F34.wireOp",VERTEX,"E38.end");
            cPlane(context, id + "F37", {"entities" : qUnion([Q0, Q1, Q2]), "cplaneType" : CPlaneType.THREE_POINT, "offset" : 150 * mm, "width" : 150 * mm, "height" : 150 * mm});
        }
        {
            var Q0;
            Q0=qCreatedBy(id+"F37.planeOp",FACE);
            var sketch = newSketch(context, id + "F38", { "sketchPlane" : qUnion([Q0])});
            skLineSegment(sketch, "E41.0", {"start": v(34.97, 0) * mm, "end": v(47.73, 0) * mm});
            skLineSegment(sketch, "E42", {"start": v(34.97, 0) * mm, "end": v(34.97, 33.61) * mm});
            skSolve(sketch);
        }
        {
            var Q0;
            Q0=makeQuery(id+"F21.opPattern","COPY",BODY,{"derivedFrom":makeQuery(id+"F16.opPattern","COPY",BODY,{"derivedFrom":makeQuery(id+"F3.opExtrude","SWEPT_BODY",BODY,{"disambiguationData":[OSD([sQuery(id+"F1.wireOp",EDGE,"E2.0"),sQuery(id+"F1.wireOp",EDGE,"E2.1"),sQuery(id+"F1.wireOp",EDGE,"E2.2"),sQuery(id+"F1.wireOp",EDGE,"E2.3"),sQuery(id+"F1.wireOp",EDGE,"E2.4"),sQuery(id+"F1.wireOp",EDGE,"E2.5")])]}),"instanceName":"1"}),"instanceName":"2"});
            var Q1;
            Q1=makeQuery(id+"F21.opPattern","COPY",BODY,{"derivedFrom":makeQuery(id+"F16.opPattern","COPY",BODY,{"derivedFrom":makeQuery(id+"F15.opPattern","COPY",BODY,{"derivedFrom":makeQuery(id+"F14.opPattern","COPY",BODY,{"derivedFrom":makeQuery(id+"F8.opExtrude","SWEPT_BODY",BODY,{"disambiguationData":[OSD([sQuery(id+"F7.wireOp",EDGE,"E7.0"),sQuery(id+"F7.wireOp",EDGE,"E10"),sQuery(id+"F7.wireOp",EDGE,"E11"),sQuery(id+"F7.wireOp",EDGE,"E12.1.0"),sQuery(id+"F7.wireOp",EDGE,"E12.1.1"),sQuery(id+"F7.wireOp",EDGE,"E12.2.0"),sQuery(id+"F7.wireOp",EDGE,"E12.2.1"),sQuery(id+"F7.wireOp",EDGE,"E12.3.0"),sQuery(id+"F7.wireOp",EDGE,"E12.3.1"),sQuery(id+"F7.wireOp",EDGE,"E12.4.0"),sQuery(id+"F7.wireOp",EDGE,"E12.4.1"),sQuery(id+"F7.wireOp",EDGE,"E12.5.0"),sQuery(id+"F7.wireOp",EDGE,"E12.5.1"),sQuery(id+"F7.wireOp",EDGE,"E12.6.0"),sQuery(id+"F7.wireOp",EDGE,"E13"),sQuery(id+"F7.wireOp",EDGE,"E14")])]}),"instanceName":"2"}),"instanceName":"1"}),"instanceName":"1"}),"instanceName":"2"});
            var Q2;
            Q2=makeQuery(id+"F21.opPattern","COPY",BODY,{"derivedFrom":makeQuery(id+"F16.opPattern","COPY",BODY,{"derivedFrom":makeQuery(id+"F12.opPattern","COPY",BODY,{"derivedFrom":makeQuery(id+"F8.opExtrude","SWEPT_BODY",BODY,{"disambiguationData":[OSD([sQuery(id+"F7.wireOp",EDGE,"E7.0"),sQuery(id+"F7.wireOp",EDGE,"E10"),sQuery(id+"F7.wireOp",EDGE,"E11"),sQuery(id+"F7.wireOp",EDGE,"E12.1.0"),sQuery(id+"F7.wireOp",EDGE,"E12.1.1"),sQuery(id+"F7.wireOp",EDGE,"E12.2.0"),sQuery(id+"F7.wireOp",EDGE,"E12.2.1"),sQuery(id+"F7.wireOp",EDGE,"E12.3.0"),sQuery(id+"F7.wireOp",EDGE,"E12.3.1"),sQuery(id+"F7.wireOp",EDGE,"E12.4.0"),sQuery(id+"F7.wireOp",EDGE,"E12.4.1"),sQuery(id+"F7.wireOp",EDGE,"E12.5.0"),sQuery(id+"F7.wireOp",EDGE,"E12.5.1"),sQuery(id+"F7.wireOp",EDGE,"E12.6.0"),sQuery(id+"F7.wireOp",EDGE,"E13"),sQuery(id+"F7.wireOp",EDGE,"E14")])]}),"instanceName":"1"}),"instanceName":"1"}),"instanceName":"2"});
            var Q3;
            Q3=makeQuery(id+"F17.opPattern","COPY",BODY,{"derivedFrom":makeQuery(id+"F12.opPattern","COPY",BODY,{"derivedFrom":makeQuery(id+"F8.opExtrude","SWEPT_BODY",BODY,{"disambiguationData":[OSD([sQuery(id+"F7.wireOp",EDGE,"E7.0"),sQuery(id+"F7.wireOp",EDGE,"E10"),sQuery(id+"F7.wireOp",EDGE,"E11"),sQuery(id+"F7.wireOp",EDGE,"E12.1.0"),sQuery(id+"F7.wireOp",EDGE,"E12.1.1"),sQuery(id+"F7.wireOp",EDGE,"E12.2.0"),sQuery(id+"F7.wireOp",EDGE,"E12.2.1"),sQuery(id+"F7.wireOp",EDGE,"E12.3.0"),sQuery(id+"F7.wireOp",EDGE,"E12.3.1"),sQuery(id+"F7.wireOp",EDGE,"E12.4.0"),sQuery(id+"F7.wireOp",EDGE,"E12.4.1"),sQuery(id+"F7.wireOp",EDGE,"E12.5.0"),sQuery(id+"F7.wireOp",EDGE,"E12.5.1"),sQuery(id+"F7.wireOp",EDGE,"E12.6.0"),sQuery(id+"F7.wireOp",EDGE,"E13"),sQuery(id+"F7.wireOp",EDGE,"E14")])]}),"instanceName":"2"}),"instanceName":"1"});
            var Q4;
            Q4=sQuery(id+"F38.wireOp",EDGE,"E42");
            circularPattern(context, id + "F39", {"entities" : qUnion([Q0, Q1, Q2, Q3]), "axis" : qUnion([Q4]), "angle" : 72 * degree, "instanceCount" : round(3), "oppositeDirection" : true});
        }
        {
            var Q0;
            Q0=makeQuery(id+"F35.opPattern","COPY",FACE,{"derivedFrom":makeQuery(id+"F2.opExtrude","CAP_FACE",FACE,{"disambiguationData":[OSD([sQuery(id+"F0.wireOp",EDGE,"E0.0"),sQuery(id+"F0.wireOp",EDGE,"E0.1"),sQuery(id+"F0.wireOp",EDGE,"E0.2"),sQuery(id+"F0.wireOp",EDGE,"E0.3"),sQuery(id+"F0.wireOp",EDGE,"E0.4")])],"isStart":true}),"instanceName":"2"});
            var sketch = newSketch(context, id + "F40", { "sketchPlane" : qUnion([Q0])});
            skLineSegment(sketch, "E43", {"start": v(-1.57, 27.68) * mm, "end": v(-4.22, 40.16) * mm});
            skPoint(sketch, "E44.orphan", {"position": v(-6.37, 50.26) * mm});
            skSolve(sketch);
        }
        {
            var Q0;
            Q0=sQuery(id+"F40.wireOp",VERTEX,"E43.end");
            var Q1;
            Q1=sQuery(id+"F40.wireOp",VERTEX,"E43.start");
            var Q2;
            Q2=sQuery(id+"F10.wireOp",VERTEX,"E16.end");
            cPlane(context, id + "F41", {"entities" : qUnion([Q0, Q1, Q2]), "cplaneType" : CPlaneType.THREE_POINT, "offset" : 150 * mm, "width" : 150 * mm, "height" : 150 * mm});
        }
        {
            var Q0;
            Q0=qCreatedBy(id+"F41.planeOp",FACE);
            var sketch = newSketch(context, id + "F42", { "sketchPlane" : qUnion([Q0])});
            skLineSegment(sketch, "E45.0", {"start": v(27.4, 0.24) * mm, "end": v(40.16, 0.63) * mm});
            skLineSegment(sketch, "E46", {"start": v(40.16, 0.63) * mm, "end": v(38.51, 53.36) * mm});
            skSolve(sketch);
        }
        {
            var Q0;
            Q0=makeQuery(id+"F39.opPattern","COPY",BODY,{"derivedFrom":makeQuery(id+"F21.opPattern","COPY",BODY,{"derivedFrom":makeQuery(id+"F16.opPattern","COPY",BODY,{"derivedFrom":makeQuery(id+"F3.opExtrude","SWEPT_BODY",BODY,{"disambiguationData":[OSD([sQuery(id+"F1.wireOp",EDGE,"E2.0"),sQuery(id+"F1.wireOp",EDGE,"E2.1"),sQuery(id+"F1.wireOp",EDGE,"E2.2"),sQuery(id+"F1.wireOp",EDGE,"E2.3"),sQuery(id+"F1.wireOp",EDGE,"E2.4"),sQuery(id+"F1.wireOp",EDGE,"E2.5")])]}),"instanceName":"1"}),"instanceName":"2"}),"instanceName":"2"});
            var Q1;
            Q1=makeQuery(id+"F39.opPattern","COPY",BODY,{"derivedFrom":makeQuery(id+"F21.opPattern","COPY",BODY,{"derivedFrom":makeQuery(id+"F16.opPattern","COPY",BODY,{"derivedFrom":makeQuery(id+"F12.opPattern","COPY",BODY,{"derivedFrom":makeQuery(id+"F8.opExtrude","SWEPT_BODY",BODY,{"disambiguationData":[OSD([sQuery(id+"F7.wireOp",EDGE,"E7.0"),sQuery(id+"F7.wireOp",EDGE,"E10"),sQuery(id+"F7.wireOp",EDGE,"E11"),sQuery(id+"F7.wireOp",EDGE,"E12.1.0"),sQuery(id+"F7.wireOp",EDGE,"E12.1.1"),sQuery(id+"F7.wireOp",EDGE,"E12.2.0"),sQuery(id+"F7.wireOp",EDGE,"E12.2.1"),sQuery(id+"F7.wireOp",EDGE,"E12.3.0"),sQuery(id+"F7.wireOp",EDGE,"E12.3.1"),sQuery(id+"F7.wireOp",EDGE,"E12.4.0"),sQuery(id+"F7.wireOp",EDGE,"E12.4.1"),sQuery(id+"F7.wireOp",EDGE,"E12.5.0"),sQuery(id+"F7.wireOp",EDGE,"E12.5.1"),sQuery(id+"F7.wireOp",EDGE,"E12.6.0"),sQuery(id+"F7.wireOp",EDGE,"E13"),sQuery(id+"F7.wireOp",EDGE,"E14")])]}),"instanceName":"1"}),"instanceName":"1"}),"instanceName":"2"}),"instanceName":"2"});
            var Q2;
            Q2=makeQuery(id+"F39.opPattern","COPY",BODY,{"derivedFrom":makeQuery(id+"F17.opPattern","COPY",BODY,{"derivedFrom":makeQuery(id+"F12.opPattern","COPY",BODY,{"derivedFrom":makeQuery(id+"F8.opExtrude","SWEPT_BODY",BODY,{"disambiguationData":[OSD([sQuery(id+"F7.wireOp",EDGE,"E7.0"),sQuery(id+"F7.wireOp",EDGE,"E10"),sQuery(id+"F7.wireOp",EDGE,"E11"),sQuery(id+"F7.wireOp",EDGE,"E12.1.0"),sQuery(id+"F7.wireOp",EDGE,"E12.1.1"),sQuery(id+"F7.wireOp",EDGE,"E12.2.0"),sQuery(id+"F7.wireOp",EDGE,"E12.2.1"),sQuery(id+"F7.wireOp",EDGE,"E12.3.0"),sQuery(id+"F7.wireOp",EDGE,"E12.3.1"),sQuery(id+"F7.wireOp",EDGE,"E12.4.0"),sQuery(id+"F7.wireOp",EDGE,"E12.4.1"),sQuery(id+"F7.wireOp",EDGE,"E12.5.0"),sQuery(id+"F7.wireOp",EDGE,"E12.5.1"),sQuery(id+"F7.wireOp",EDGE,"E12.6.0"),sQuery(id+"F7.wireOp",EDGE,"E13"),sQuery(id+"F7.wireOp",EDGE,"E14")])]}),"instanceName":"2"}),"instanceName":"1"}),"instanceName":"2"});
            var Q3;
            Q3=makeQuery(id+"F39.opPattern","COPY",BODY,{"derivedFrom":makeQuery(id+"F21.opPattern","COPY",BODY,{"derivedFrom":makeQuery(id+"F16.opPattern","COPY",BODY,{"derivedFrom":makeQuery(id+"F15.opPattern","COPY",BODY,{"derivedFrom":makeQuery(id+"F14.opPattern","COPY",BODY,{"derivedFrom":makeQuery(id+"F8.opExtrude","SWEPT_BODY",BODY,{"disambiguationData":[OSD([sQuery(id+"F7.wireOp",EDGE,"E7.0"),sQuery(id+"F7.wireOp",EDGE,"E10"),sQuery(id+"F7.wireOp",EDGE,"E11"),sQuery(id+"F7.wireOp",EDGE,"E12.1.0"),sQuery(id+"F7.wireOp",EDGE,"E12.1.1"),sQuery(id+"F7.wireOp",EDGE,"E12.2.0"),sQuery(id+"F7.wireOp",EDGE,"E12.2.1"),sQuery(id+"F7.wireOp",EDGE,"E12.3.0"),sQuery(id+"F7.wireOp",EDGE,"E12.3.1"),sQuery(id+"F7.wireOp",EDGE,"E12.4.0"),sQuery(id+"F7.wireOp",EDGE,"E12.4.1"),sQuery(id+"F7.wireOp",EDGE,"E12.5.0"),sQuery(id+"F7.wireOp",EDGE,"E12.5.1"),sQuery(id+"F7.wireOp",EDGE,"E12.6.0"),sQuery(id+"F7.wireOp",EDGE,"E13"),sQuery(id+"F7.wireOp",EDGE,"E14")])]}),"instanceName":"2"}),"instanceName":"1"}),"instanceName":"1"}),"instanceName":"2"}),"instanceName":"2"});
            var Q4;
            Q4=sQuery(id+"F42.wireOp",EDGE,"E46");
            circularPattern(context, id + "F43", {"entities" : qUnion([Q0, Q1, Q2, Q3]), "axis" : qUnion([Q4]), "angle" : 72 * degree, "instanceCount" : round(3), "oppositeDirection" : true});
        }
        {
            var Q0;
            Q0=makeQuery(id+"F39.opPattern","COPY",FACE,{"derivedFrom":makeQuery(id+"F21.opPattern","COPY",FACE,{"derivedFrom":makeQuery(id+"F16.opPattern","COPY",FACE,{"derivedFrom":makeQuery(id+"F3.opExtrude","CAP_FACE",FACE,{"disambiguationData":[OSD([sQuery(id+"F1.wireOp",EDGE,"E2.0"),sQuery(id+"F1.wireOp",EDGE,"E2.1"),sQuery(id+"F1.wireOp",EDGE,"E2.2"),sQuery(id+"F1.wireOp",EDGE,"E2.3"),sQuery(id+"F1.wireOp",EDGE,"E2.4"),sQuery(id+"F1.wireOp",EDGE,"E2.5")])],"isStart":true}),"instanceName":"1"}),"instanceName":"2"}),"instanceName":"1"});
            var sketch = newSketch(context, id + "F44", { "sketchPlane" : qUnion([Q0])});
            skLineSegment(sketch, "E47", {"start": v(-79.28, 20.24) * mm, "end": v(-78.5, 7.27) * mm});
            skSolve(sketch);
        }
        {
            var Q0;
            Q0=sQuery(id+"F44.wireOp",VERTEX,"E47.end");
            var Q1;
            Q1=sQuery(id+"F44.wireOp",VERTEX,"E47.start");
            var Q2;
            Q2=makeQuery(id+"F5.opPattern","COPY",VERTEX,{"derivedFrom":makeQuery(id+"F3.opExtrude","CAP_VERTEX",VERTEX,{"disambiguationData":[OSD([sQuery(id+"F1.wireOp",EDGE,"E2.1"),sQuery(id+"F1.wireOp",EDGE,"E2.2")])],"isStart":true}),"instanceName":"3"});
            cPlane(context, id + "F45", {"entities" : qUnion([Q0, Q1, Q2]), "cplaneType" : CPlaneType.THREE_POINT, "offset" : 150 * mm, "width" : 150 * mm, "height" : 150 * mm});
        }
        {
            var Q0;
            Q0=qCreatedBy(id+"F45.planeOp",FACE);
            var sketch = newSketch(context, id + "F46", { "sketchPlane" : qUnion([Q0])});
            skLineSegment(sketch, "E48.0", {"start": v(-79.28, 20.24) * mm, "end": v(-78.5, 7.27) * mm});
            skLineSegment(sketch, "E49", {"start": v(-78.5, 7.27) * mm, "end": v(-107.45, 5.5) * mm});
            skSolve(sketch);
        }
        {
            var Q0;
            Q0=makeQuery(id+"F21.opPattern","COPY",BODY,{"derivedFrom":makeQuery(id+"F16.opPattern","COPY",BODY,{"derivedFrom":makeQuery(id+"F3.opExtrude","SWEPT_BODY",BODY,{"disambiguationData":[OSD([sQuery(id+"F1.wireOp",EDGE,"E2.0"),sQuery(id+"F1.wireOp",EDGE,"E2.1"),sQuery(id+"F1.wireOp",EDGE,"E2.2"),sQuery(id+"F1.wireOp",EDGE,"E2.3"),sQuery(id+"F1.wireOp",EDGE,"E2.4"),sQuery(id+"F1.wireOp",EDGE,"E2.5")])]}),"instanceName":"1"}),"instanceName":"2"});
            var Q1;
            Q1=makeQuery(id+"F21.opPattern","COPY",BODY,{"derivedFrom":makeQuery(id+"F16.opPattern","COPY",BODY,{"derivedFrom":makeQuery(id+"F12.opPattern","COPY",BODY,{"derivedFrom":makeQuery(id+"F8.opExtrude","SWEPT_BODY",BODY,{"disambiguationData":[OSD([sQuery(id+"F7.wireOp",EDGE,"E7.0"),sQuery(id+"F7.wireOp",EDGE,"E10"),sQuery(id+"F7.wireOp",EDGE,"E11"),sQuery(id+"F7.wireOp",EDGE,"E12.1.0"),sQuery(id+"F7.wireOp",EDGE,"E12.1.1"),sQuery(id+"F7.wireOp",EDGE,"E12.2.0"),sQuery(id+"F7.wireOp",EDGE,"E12.2.1"),sQuery(id+"F7.wireOp",EDGE,"E12.3.0"),sQuery(id+"F7.wireOp",EDGE,"E12.3.1"),sQuery(id+"F7.wireOp",EDGE,"E12.4.0"),sQuery(id+"F7.wireOp",EDGE,"E12.4.1"),sQuery(id+"F7.wireOp",EDGE,"E12.5.0"),sQuery(id+"F7.wireOp",EDGE,"E12.5.1"),sQuery(id+"F7.wireOp",EDGE,"E12.6.0"),sQuery(id+"F7.wireOp",EDGE,"E13"),sQuery(id+"F7.wireOp",EDGE,"E14")])]}),"instanceName":"1"}),"instanceName":"1"}),"instanceName":"2"});
            var Q2;
            Q2=makeQuery(id+"F21.opPattern","COPY",BODY,{"derivedFrom":makeQuery(id+"F16.opPattern","COPY",BODY,{"derivedFrom":makeQuery(id+"F15.opPattern","COPY",BODY,{"derivedFrom":makeQuery(id+"F14.opPattern","COPY",BODY,{"derivedFrom":makeQuery(id+"F8.opExtrude","SWEPT_BODY",BODY,{"disambiguationData":[OSD([sQuery(id+"F7.wireOp",EDGE,"E7.0"),sQuery(id+"F7.wireOp",EDGE,"E10"),sQuery(id+"F7.wireOp",EDGE,"E11"),sQuery(id+"F7.wireOp",EDGE,"E12.1.0"),sQuery(id+"F7.wireOp",EDGE,"E12.1.1"),sQuery(id+"F7.wireOp",EDGE,"E12.2.0"),sQuery(id+"F7.wireOp",EDGE,"E12.2.1"),sQuery(id+"F7.wireOp",EDGE,"E12.3.0"),sQuery(id+"F7.wireOp",EDGE,"E12.3.1"),sQuery(id+"F7.wireOp",EDGE,"E12.4.0"),sQuery(id+"F7.wireOp",EDGE,"E12.4.1"),sQuery(id+"F7.wireOp",EDGE,"E12.5.0"),sQuery(id+"F7.wireOp",EDGE,"E12.5.1"),sQuery(id+"F7.wireOp",EDGE,"E12.6.0"),sQuery(id+"F7.wireOp",EDGE,"E13"),sQuery(id+"F7.wireOp",EDGE,"E14")])]}),"instanceName":"2"}),"instanceName":"1"}),"instanceName":"1"}),"instanceName":"2"});
            var Q3;
            Q3=makeQuery(id+"F17.opPattern","COPY",BODY,{"derivedFrom":makeQuery(id+"F12.opPattern","COPY",BODY,{"derivedFrom":makeQuery(id+"F8.opExtrude","SWEPT_BODY",BODY,{"disambiguationData":[OSD([sQuery(id+"F7.wireOp",EDGE,"E7.0"),sQuery(id+"F7.wireOp",EDGE,"E10"),sQuery(id+"F7.wireOp",EDGE,"E11"),sQuery(id+"F7.wireOp",EDGE,"E12.1.0"),sQuery(id+"F7.wireOp",EDGE,"E12.1.1"),sQuery(id+"F7.wireOp",EDGE,"E12.2.0"),sQuery(id+"F7.wireOp",EDGE,"E12.2.1"),sQuery(id+"F7.wireOp",EDGE,"E12.3.0"),sQuery(id+"F7.wireOp",EDGE,"E12.3.1"),sQuery(id+"F7.wireOp",EDGE,"E12.4.0"),sQuery(id+"F7.wireOp",EDGE,"E12.4.1"),sQuery(id+"F7.wireOp",EDGE,"E12.5.0"),sQuery(id+"F7.wireOp",EDGE,"E12.5.1"),sQuery(id+"F7.wireOp",EDGE,"E12.6.0"),sQuery(id+"F7.wireOp",EDGE,"E13"),sQuery(id+"F7.wireOp",EDGE,"E14")])]}),"instanceName":"2"}),"instanceName":"1"});
            var Q4;
            Q4=sQuery(id+"F46.wireOp",EDGE,"E49");
            circularPattern(context, id + "F47", {"entities" : qUnion([Q0, Q1, Q2, Q3]), "axis" : qUnion([Q4]), "angle" : 120 * degree, "instanceCount" : 2, "oppositeDirection" : true});
        }
        {
            var Q0;
            Q0=makeQuery(id+"F25.opPattern","COPY",FACE,{"derivedFrom":makeQuery(id+"F3.opExtrude","CAP_FACE",FACE,{"disambiguationData":[OSD([sQuery(id+"F1.wireOp",EDGE,"E2.0"),sQuery(id+"F1.wireOp",EDGE,"E2.1"),sQuery(id+"F1.wireOp",EDGE,"E2.2"),sQuery(id+"F1.wireOp",EDGE,"E2.3"),sQuery(id+"F1.wireOp",EDGE,"E2.4"),sQuery(id+"F1.wireOp",EDGE,"E2.5")])],"isStart":true}),"instanceName":"1"});
            var sketch = newSketch(context, id + "F48", { "sketchPlane" : qUnion([Q0])});
            skLineSegment(sketch, "E50", {"start": v(32.54, -36.3) * mm, "end": v(43.38, -43.46) * mm});
            skSolve(sketch);
        }
        {
            var Q0;
            Q0=sQuery(id+"F48.wireOp",VERTEX,"E50.end");
            var Q1;
            Q1=sQuery(id+"F48.wireOp",VERTEX,"E50.start");
            var Q2;
            Q2=makeQuery(id+"F5.opPattern","COPY",VERTEX,{"derivedFrom":makeQuery(id+"F3.opExtrude","CAP_VERTEX",VERTEX,{"disambiguationData":[OSD([sQuery(id+"F1.wireOp",EDGE,"E2.0"),sQuery(id+"F1.wireOp",EDGE,"E2.5")])],"isStart":true}),"instanceName":"4"});
            cPlane(context, id + "F49", {"entities" : qUnion([Q0, Q1, Q2]), "cplaneType" : CPlaneType.THREE_POINT, "offset" : 150 * mm, "width" : 150 * mm, "height" : 150 * mm});
        }
        {
            var Q0;
            Q0=qCreatedBy(id+"F49.planeOp",FACE);
            var sketch = newSketch(context, id + "F50", { "sketchPlane" : qUnion([Q0])});
            skLineSegment(sketch, "E51.0", {"start": v(32.54, 36.3) * mm, "end": v(43.38, 43.46) * mm});
            skLineSegment(sketch, "E52", {"start": v(43.38, 43.46) * mm, "end": v(66.29, 8.83) * mm});
            skSolve(sketch);
        }
        {
            var Q0;
            Q0=makeQuery(id+"F15.opPattern","COPY",BODY,{"derivedFrom":makeQuery(id+"F14.opPattern","COPY",BODY,{"derivedFrom":makeQuery(id+"F8.opExtrude","SWEPT_BODY",BODY,{"disambiguationData":[OSD([sQuery(id+"F7.wireOp",EDGE,"E7.0"),sQuery(id+"F7.wireOp",EDGE,"E10"),sQuery(id+"F7.wireOp",EDGE,"E11"),sQuery(id+"F7.wireOp",EDGE,"E12.1.0"),sQuery(id+"F7.wireOp",EDGE,"E12.1.1"),sQuery(id+"F7.wireOp",EDGE,"E12.2.0"),sQuery(id+"F7.wireOp",EDGE,"E12.2.1"),sQuery(id+"F7.wireOp",EDGE,"E12.3.0"),sQuery(id+"F7.wireOp",EDGE,"E12.3.1"),sQuery(id+"F7.wireOp",EDGE,"E12.4.0"),sQuery(id+"F7.wireOp",EDGE,"E12.4.1"),sQuery(id+"F7.wireOp",EDGE,"E12.5.0"),sQuery(id+"F7.wireOp",EDGE,"E12.5.1"),sQuery(id+"F7.wireOp",EDGE,"E12.6.0"),sQuery(id+"F7.wireOp",EDGE,"E13"),sQuery(id+"F7.wireOp",EDGE,"E14")])]}),"instanceName":"1"}),"instanceName":"1"});
            var Q1;
            Q1=makeQuery(id+"F12.opPattern","COPY",BODY,{"derivedFrom":makeQuery(id+"F8.opExtrude","SWEPT_BODY",BODY,{"disambiguationData":[OSD([sQuery(id+"F7.wireOp",EDGE,"E7.0"),sQuery(id+"F7.wireOp",EDGE,"E10"),sQuery(id+"F7.wireOp",EDGE,"E11"),sQuery(id+"F7.wireOp",EDGE,"E12.1.0"),sQuery(id+"F7.wireOp",EDGE,"E12.1.1"),sQuery(id+"F7.wireOp",EDGE,"E12.2.0"),sQuery(id+"F7.wireOp",EDGE,"E12.2.1"),sQuery(id+"F7.wireOp",EDGE,"E12.3.0"),sQuery(id+"F7.wireOp",EDGE,"E12.3.1"),sQuery(id+"F7.wireOp",EDGE,"E12.4.0"),sQuery(id+"F7.wireOp",EDGE,"E12.4.1"),sQuery(id+"F7.wireOp",EDGE,"E12.5.0"),sQuery(id+"F7.wireOp",EDGE,"E12.5.1"),sQuery(id+"F7.wireOp",EDGE,"E12.6.0"),sQuery(id+"F7.wireOp",EDGE,"E13"),sQuery(id+"F7.wireOp",EDGE,"E14")])]}),"instanceName":"1"});
            var Q2;
            Q2=makeQuery(id+"F15.opPattern","COPY",BODY,{"derivedFrom":makeQuery(id+"F14.opPattern","COPY",BODY,{"derivedFrom":makeQuery(id+"F8.opExtrude","SWEPT_BODY",BODY,{"disambiguationData":[OSD([sQuery(id+"F7.wireOp",EDGE,"E7.0"),sQuery(id+"F7.wireOp",EDGE,"E10"),sQuery(id+"F7.wireOp",EDGE,"E11"),sQuery(id+"F7.wireOp",EDGE,"E12.1.0"),sQuery(id+"F7.wireOp",EDGE,"E12.1.1"),sQuery(id+"F7.wireOp",EDGE,"E12.2.0"),sQuery(id+"F7.wireOp",EDGE,"E12.2.1"),sQuery(id+"F7.wireOp",EDGE,"E12.3.0"),sQuery(id+"F7.wireOp",EDGE,"E12.3.1"),sQuery(id+"F7.wireOp",EDGE,"E12.4.0"),sQuery(id+"F7.wireOp",EDGE,"E12.4.1"),sQuery(id+"F7.wireOp",EDGE,"E12.5.0"),sQuery(id+"F7.wireOp",EDGE,"E12.5.1"),sQuery(id+"F7.wireOp",EDGE,"E12.6.0"),sQuery(id+"F7.wireOp",EDGE,"E13"),sQuery(id+"F7.wireOp",EDGE,"E14")])]}),"instanceName":"2"}),"instanceName":"1"});
            var Q3;
            Q3=makeQuery(id+"F3.opExtrude","SWEPT_BODY",BODY,{"disambiguationData":[OSD([sQuery(id+"F1.wireOp",EDGE,"E2.0"),sQuery(id+"F1.wireOp",EDGE,"E2.1"),sQuery(id+"F1.wireOp",EDGE,"E2.2"),sQuery(id+"F1.wireOp",EDGE,"E2.3"),sQuery(id+"F1.wireOp",EDGE,"E2.4"),sQuery(id+"F1.wireOp",EDGE,"E2.5")])]});
            var Q4;
            Q4=sQuery(id+"F50.wireOp",EDGE,"E52");
            circularPattern(context, id + "F51", {"entities" : qUnion([Q0, Q1, Q2, Q3]), "axis" : qUnion([Q4]), "angle" : 120 * degree, "instanceCount" : round(2), "oppositeDirection" : true});
        }
        {
            var Q0;
            Q0=makeQuery(id+"F31.opPattern","COPY",FACE,{"derivedFrom":makeQuery(id+"F25.opPattern","COPY",FACE,{"derivedFrom":makeQuery(id+"F3.opExtrude","CAP_FACE",FACE,{"disambiguationData":[OSD([sQuery(id+"F1.wireOp",EDGE,"E2.0"),sQuery(id+"F1.wireOp",EDGE,"E2.1"),sQuery(id+"F1.wireOp",EDGE,"E2.2"),sQuery(id+"F1.wireOp",EDGE,"E2.3"),sQuery(id+"F1.wireOp",EDGE,"E2.4"),sQuery(id+"F1.wireOp",EDGE,"E2.5")])],"isStart":true}),"instanceName":"2"}),"instanceName":"1"});
            var sketch = newSketch(context, id + "F52", { "sketchPlane" : qUnion([Q0])});
            skLineSegment(sketch, "E53", {"start": v(-16.15, -29.57) * mm, "end": v(-16.15, -14.57) * mm});
            skSolve(sketch);
        }
        {
            var Q0;
            Q0=sQuery(id+"F52.wireOp",VERTEX,"E53.start");
            var Q1;
            Q1=sQuery(id+"F52.wireOp",VERTEX,"E53.end");
            var Q2;
            Q2=makeQuery(id+"F31.opPattern","COPY",VERTEX,{"derivedFrom":makeQuery(id+"F25.opPattern","COPY",VERTEX,{"derivedFrom":makeQuery(id+"F3.opExtrude","CAP_VERTEX",VERTEX,{"disambiguationData":[OSD([sQuery(id+"F1.wireOp",EDGE,"E2.2"),sQuery(id+"F1.wireOp",EDGE,"E2.3")])],"isStart":false}),"instanceName":"2"}),"instanceName":"1"});
            cPlane(context, id + "F53", {"entities" : qUnion([Q0, Q1, Q2]), "cplaneType" : CPlaneType.THREE_POINT, "offset" : 150 * mm, "width" : 150 * mm, "height" : 150 * mm});
        }
        {
            var Q0;
            Q0=qCreatedBy(id+"F53.planeOp",FACE);
            var sketch = newSketch(context, id + "F54", { "sketchPlane" : qUnion([Q0])});
            skLineSegment(sketch, "E54.0", {"start": v(-29.57, 0) * mm, "end": v(-14.57, 0) * mm});
            skLineSegment(sketch, "E55", {"start": v(-14.57, 0) * mm, "end": v(-14.57, -45.42) * mm});
            skSolve(sketch);
        }
        {
            var Q0;
            Q0=makeQuery(id+"F25.opPattern","COPY",BODY,{"derivedFrom":makeQuery(id+"F3.opExtrude","SWEPT_BODY",BODY,{"disambiguationData":[OSD([sQuery(id+"F1.wireOp",EDGE,"E2.0"),sQuery(id+"F1.wireOp",EDGE,"E2.1"),sQuery(id+"F1.wireOp",EDGE,"E2.2"),sQuery(id+"F1.wireOp",EDGE,"E2.3"),sQuery(id+"F1.wireOp",EDGE,"E2.4"),sQuery(id+"F1.wireOp",EDGE,"E2.5")])]}),"instanceName":"2"});
            var Q1;
            Q1=makeQuery(id+"F25.opPattern","COPY",BODY,{"derivedFrom":makeQuery(id+"F15.opPattern","COPY",BODY,{"derivedFrom":makeQuery(id+"F14.opPattern","COPY",BODY,{"derivedFrom":makeQuery(id+"F8.opExtrude","SWEPT_BODY",BODY,{"disambiguationData":[OSD([sQuery(id+"F7.wireOp",EDGE,"E7.0"),sQuery(id+"F7.wireOp",EDGE,"E10"),sQuery(id+"F7.wireOp",EDGE,"E11"),sQuery(id+"F7.wireOp",EDGE,"E12.1.0"),sQuery(id+"F7.wireOp",EDGE,"E12.1.1"),sQuery(id+"F7.wireOp",EDGE,"E12.2.0"),sQuery(id+"F7.wireOp",EDGE,"E12.2.1"),sQuery(id+"F7.wireOp",EDGE,"E12.3.0"),sQuery(id+"F7.wireOp",EDGE,"E12.3.1"),sQuery(id+"F7.wireOp",EDGE,"E12.4.0"),sQuery(id+"F7.wireOp",EDGE,"E12.4.1"),sQuery(id+"F7.wireOp",EDGE,"E12.5.0"),sQuery(id+"F7.wireOp",EDGE,"E12.5.1"),sQuery(id+"F7.wireOp",EDGE,"E12.6.0"),sQuery(id+"F7.wireOp",EDGE,"E13"),sQuery(id+"F7.wireOp",EDGE,"E14")])]}),"instanceName":"2"}),"instanceName":"1"}),"instanceName":"2"});
            var Q2;
            Q2=makeQuery(id+"F25.opPattern","COPY",BODY,{"derivedFrom":makeQuery(id+"F12.opPattern","COPY",BODY,{"derivedFrom":makeQuery(id+"F8.opExtrude","SWEPT_BODY",BODY,{"disambiguationData":[OSD([sQuery(id+"F7.wireOp",EDGE,"E7.0"),sQuery(id+"F7.wireOp",EDGE,"E10"),sQuery(id+"F7.wireOp",EDGE,"E11"),sQuery(id+"F7.wireOp",EDGE,"E12.1.0"),sQuery(id+"F7.wireOp",EDGE,"E12.1.1"),sQuery(id+"F7.wireOp",EDGE,"E12.2.0"),sQuery(id+"F7.wireOp",EDGE,"E12.2.1"),sQuery(id+"F7.wireOp",EDGE,"E12.3.0"),sQuery(id+"F7.wireOp",EDGE,"E12.3.1"),sQuery(id+"F7.wireOp",EDGE,"E12.4.0"),sQuery(id+"F7.wireOp",EDGE,"E12.4.1"),sQuery(id+"F7.wireOp",EDGE,"E12.5.0"),sQuery(id+"F7.wireOp",EDGE,"E12.5.1"),sQuery(id+"F7.wireOp",EDGE,"E12.6.0"),sQuery(id+"F7.wireOp",EDGE,"E13"),sQuery(id+"F7.wireOp",EDGE,"E14")])]}),"instanceName":"1"}),"instanceName":"2"});
            var Q3;
            Q3=makeQuery(id+"F17.opPattern","COPY",BODY,{"derivedFrom":makeQuery(id+"F12.opPattern","COPY",BODY,{"derivedFrom":makeQuery(id+"F8.opExtrude","SWEPT_BODY",BODY,{"disambiguationData":[OSD([sQuery(id+"F7.wireOp",EDGE,"E7.0"),sQuery(id+"F7.wireOp",EDGE,"E10"),sQuery(id+"F7.wireOp",EDGE,"E11"),sQuery(id+"F7.wireOp",EDGE,"E12.1.0"),sQuery(id+"F7.wireOp",EDGE,"E12.1.1"),sQuery(id+"F7.wireOp",EDGE,"E12.2.0"),sQuery(id+"F7.wireOp",EDGE,"E12.2.1"),sQuery(id+"F7.wireOp",EDGE,"E12.3.0"),sQuery(id+"F7.wireOp",EDGE,"E12.3.1"),sQuery(id+"F7.wireOp",EDGE,"E12.4.0"),sQuery(id+"F7.wireOp",EDGE,"E12.4.1"),sQuery(id+"F7.wireOp",EDGE,"E12.5.0"),sQuery(id+"F7.wireOp",EDGE,"E12.5.1"),sQuery(id+"F7.wireOp",EDGE,"E12.6.0"),sQuery(id+"F7.wireOp",EDGE,"E13"),sQuery(id+"F7.wireOp",EDGE,"E14")])]}),"instanceName":"2"}),"instanceName":"2"});
            var Q4;
            Q4=sQuery(id+"F54.wireOp",EDGE,"E55");
            circularPattern(context, id + "F55", {"entities" : qUnion([Q0, Q1, Q2, Q3]), "axis" : qUnion([Q4]), "angle" : 120 * degree, "instanceCount" : 2, "oppositeDirection" : true});
        }
        {
            var Q0;
            Q0=makeQuery(id+"F55.opPattern","COPY",FACE,{"derivedFrom":makeQuery(id+"F25.opPattern","COPY",FACE,{"derivedFrom":makeQuery(id+"F3.opExtrude","CAP_FACE",FACE,{"disambiguationData":[OSD([sQuery(id+"F1.wireOp",EDGE,"E2.0"),sQuery(id+"F1.wireOp",EDGE,"E2.1"),sQuery(id+"F1.wireOp",EDGE,"E2.2"),sQuery(id+"F1.wireOp",EDGE,"E2.3"),sQuery(id+"F1.wireOp",EDGE,"E2.4"),sQuery(id+"F1.wireOp",EDGE,"E2.5")])],"isStart":true}),"instanceName":"2"}),"instanceName":"1"});
            var sketch = newSketch(context, id + "F56", { "sketchPlane" : qUnion([Q0])});
            skLineSegment(sketch, "E56", {"start": v(-16.35, 49.02) * mm, "end": v(-1.49, 51.05) * mm});
            skSolve(sketch);
        }
        {
            var Q0;
            Q0=sQuery(id+"F56.wireOp",VERTEX,"E56.start");
            var Q1;
            Q1=sQuery(id+"F56.wireOp",VERTEX,"E56.end");
            var Q2;
            Q2=makeQuery(id+"F55.opPattern","COPY",VERTEX,{"derivedFrom":makeQuery(id+"F25.opPattern","COPY",VERTEX,{"derivedFrom":makeQuery(id+"F3.opExtrude","CAP_VERTEX",VERTEX,{"disambiguationData":[OSD([sQuery(id+"F1.wireOp",EDGE,"E2.2"),sQuery(id+"F1.wireOp",EDGE,"E2.3")])],"isStart":false}),"instanceName":"2"}),"instanceName":"1"});
            cPlane(context, id + "F57", {"entities" : qUnion([Q0, Q1, Q2]), "cplaneType" : CPlaneType.THREE_POINT, "offset" : 150 * mm, "width" : 150 * mm, "height" : 150 * mm});
        }
        {
            var Q0;
            Q0=qCreatedBy(id+"F57.planeOp",FACE);
            var sketch = newSketch(context, id + "F58", { "sketchPlane" : qUnion([Q0])});
            skLineSegment(sketch, "E57.0", {"start": v(-9.58, 0) * mm, "end": v(5.42, 0) * mm});
            skLineSegment(sketch, "E58", {"start": v(5.42, 0) * mm, "end": v(5.42, -15.82) * mm});
            skSolve(sketch);
        }
        {
            var Q0;
            Q0=makeQuery(id+"F51.opPattern","COPY",BODY,{"derivedFrom":makeQuery(id+"F3.opExtrude","SWEPT_BODY",BODY,{"disambiguationData":[OSD([sQuery(id+"F1.wireOp",EDGE,"E2.0"),sQuery(id+"F1.wireOp",EDGE,"E2.1"),sQuery(id+"F1.wireOp",EDGE,"E2.2"),sQuery(id+"F1.wireOp",EDGE,"E2.3"),sQuery(id+"F1.wireOp",EDGE,"E2.4"),sQuery(id+"F1.wireOp",EDGE,"E2.5")])]}),"instanceName":"1"});
            var Q1;
            Q1=makeQuery(id+"F51.opPattern","COPY",BODY,{"derivedFrom":makeQuery(id+"F15.opPattern","COPY",BODY,{"derivedFrom":makeQuery(id+"F14.opPattern","COPY",BODY,{"derivedFrom":makeQuery(id+"F8.opExtrude","SWEPT_BODY",BODY,{"disambiguationData":[OSD([sQuery(id+"F7.wireOp",EDGE,"E7.0"),sQuery(id+"F7.wireOp",EDGE,"E10"),sQuery(id+"F7.wireOp",EDGE,"E11"),sQuery(id+"F7.wireOp",EDGE,"E12.1.0"),sQuery(id+"F7.wireOp",EDGE,"E12.1.1"),sQuery(id+"F7.wireOp",EDGE,"E12.2.0"),sQuery(id+"F7.wireOp",EDGE,"E12.2.1"),sQuery(id+"F7.wireOp",EDGE,"E12.3.0"),sQuery(id+"F7.wireOp",EDGE,"E12.3.1"),sQuery(id+"F7.wireOp",EDGE,"E12.4.0"),sQuery(id+"F7.wireOp",EDGE,"E12.4.1"),sQuery(id+"F7.wireOp",EDGE,"E12.5.0"),sQuery(id+"F7.wireOp",EDGE,"E12.5.1"),sQuery(id+"F7.wireOp",EDGE,"E12.6.0"),sQuery(id+"F7.wireOp",EDGE,"E13"),sQuery(id+"F7.wireOp",EDGE,"E14")])]}),"instanceName":"2"}),"instanceName":"1"}),"instanceName":"1"});
            var Q2;
            Q2=makeQuery(id+"F51.opPattern","COPY",BODY,{"derivedFrom":makeQuery(id+"F15.opPattern","COPY",BODY,{"derivedFrom":makeQuery(id+"F14.opPattern","COPY",BODY,{"derivedFrom":makeQuery(id+"F8.opExtrude","SWEPT_BODY",BODY,{"disambiguationData":[OSD([sQuery(id+"F7.wireOp",EDGE,"E7.0"),sQuery(id+"F7.wireOp",EDGE,"E10"),sQuery(id+"F7.wireOp",EDGE,"E11"),sQuery(id+"F7.wireOp",EDGE,"E12.1.0"),sQuery(id+"F7.wireOp",EDGE,"E12.1.1"),sQuery(id+"F7.wireOp",EDGE,"E12.2.0"),sQuery(id+"F7.wireOp",EDGE,"E12.2.1"),sQuery(id+"F7.wireOp",EDGE,"E12.3.0"),sQuery(id+"F7.wireOp",EDGE,"E12.3.1"),sQuery(id+"F7.wireOp",EDGE,"E12.4.0"),sQuery(id+"F7.wireOp",EDGE,"E12.4.1"),sQuery(id+"F7.wireOp",EDGE,"E12.5.0"),sQuery(id+"F7.wireOp",EDGE,"E12.5.1"),sQuery(id+"F7.wireOp",EDGE,"E12.6.0"),sQuery(id+"F7.wireOp",EDGE,"E13"),sQuery(id+"F7.wireOp",EDGE,"E14")])]}),"instanceName":"1"}),"instanceName":"1"}),"instanceName":"1"});
            var Q3;
            Q3=makeQuery(id+"F51.opPattern","COPY",BODY,{"derivedFrom":makeQuery(id+"F12.opPattern","COPY",BODY,{"derivedFrom":makeQuery(id+"F8.opExtrude","SWEPT_BODY",BODY,{"disambiguationData":[OSD([sQuery(id+"F7.wireOp",EDGE,"E7.0"),sQuery(id+"F7.wireOp",EDGE,"E10"),sQuery(id+"F7.wireOp",EDGE,"E11"),sQuery(id+"F7.wireOp",EDGE,"E12.1.0"),sQuery(id+"F7.wireOp",EDGE,"E12.1.1"),sQuery(id+"F7.wireOp",EDGE,"E12.2.0"),sQuery(id+"F7.wireOp",EDGE,"E12.2.1"),sQuery(id+"F7.wireOp",EDGE,"E12.3.0"),sQuery(id+"F7.wireOp",EDGE,"E12.3.1"),sQuery(id+"F7.wireOp",EDGE,"E12.4.0"),sQuery(id+"F7.wireOp",EDGE,"E12.4.1"),sQuery(id+"F7.wireOp",EDGE,"E12.5.0"),sQuery(id+"F7.wireOp",EDGE,"E12.5.1"),sQuery(id+"F7.wireOp",EDGE,"E12.6.0"),sQuery(id+"F7.wireOp",EDGE,"E13"),sQuery(id+"F7.wireOp",EDGE,"E14")])]}),"instanceName":"1"}),"instanceName":"1"});
            var Q4;
            Q4=sQuery(id+"F58.wireOp",EDGE,"E58");
            circularPattern(context, id + "F59", {"entities" : qUnion([Q0, Q1, Q2, Q3]), "axis" : qUnion([Q4]), "angle" : 120 * degree, "instanceCount" : 2, "oppositeDirection" : true});
        }
        {
            var Q0;
            Q0=makeQuery(id+"F21.opPattern","COPY",BODY,{"derivedFrom":makeQuery(id+"F16.opPattern","COPY",BODY,{"derivedFrom":makeQuery(id+"F15.opPattern","COPY",BODY,{"derivedFrom":makeQuery(id+"F14.opPattern","COPY",BODY,{"derivedFrom":makeQuery(id+"F8.opExtrude","SWEPT_BODY",BODY,{"disambiguationData":[OSD([sQuery(id+"F7.wireOp",EDGE,"E7.0"),sQuery(id+"F7.wireOp",EDGE,"E10"),sQuery(id+"F7.wireOp",EDGE,"E11"),sQuery(id+"F7.wireOp",EDGE,"E12.1.0"),sQuery(id+"F7.wireOp",EDGE,"E12.1.1"),sQuery(id+"F7.wireOp",EDGE,"E12.2.0"),sQuery(id+"F7.wireOp",EDGE,"E12.2.1"),sQuery(id+"F7.wireOp",EDGE,"E12.3.0"),sQuery(id+"F7.wireOp",EDGE,"E12.3.1"),sQuery(id+"F7.wireOp",EDGE,"E12.4.0"),sQuery(id+"F7.wireOp",EDGE,"E12.4.1"),sQuery(id+"F7.wireOp",EDGE,"E12.5.0"),sQuery(id+"F7.wireOp",EDGE,"E12.5.1"),sQuery(id+"F7.wireOp",EDGE,"E12.6.0"),sQuery(id+"F7.wireOp",EDGE,"E13"),sQuery(id+"F7.wireOp",EDGE,"E14")])]}),"instanceName":"1"}),"instanceName":"1"}),"instanceName":"1"}),"instanceName":"1"});
            deleteBodies(context, id + "F60", {"entities" : qUnion([Q0])});
        }
        {
            var Q0;
            Q0=makeQuery(id+"F21.opPattern","COPY",BODY,{"derivedFrom":makeQuery(id+"F16.opPattern","COPY",BODY,{"derivedFrom":makeQuery(id+"F15.opPattern","COPY",BODY,{"derivedFrom":makeQuery(id+"F14.opPattern","COPY",BODY,{"derivedFrom":makeQuery(id+"F8.opExtrude","SWEPT_BODY",BODY,{"disambiguationData":[OSD([sQuery(id+"F7.wireOp",EDGE,"E7.0"),sQuery(id+"F7.wireOp",EDGE,"E10"),sQuery(id+"F7.wireOp",EDGE,"E11"),sQuery(id+"F7.wireOp",EDGE,"E12.1.0"),sQuery(id+"F7.wireOp",EDGE,"E12.1.1"),sQuery(id+"F7.wireOp",EDGE,"E12.2.0"),sQuery(id+"F7.wireOp",EDGE,"E12.2.1"),sQuery(id+"F7.wireOp",EDGE,"E12.3.0"),sQuery(id+"F7.wireOp",EDGE,"E12.3.1"),sQuery(id+"F7.wireOp",EDGE,"E12.4.0"),sQuery(id+"F7.wireOp",EDGE,"E12.4.1"),sQuery(id+"F7.wireOp",EDGE,"E12.5.0"),sQuery(id+"F7.wireOp",EDGE,"E12.5.1"),sQuery(id+"F7.wireOp",EDGE,"E12.6.0"),sQuery(id+"F7.wireOp",EDGE,"E13"),sQuery(id+"F7.wireOp",EDGE,"E14")])]}),"instanceName":"1"}),"instanceName":"1"}),"instanceName":"1"}),"instanceName":"2"});
            deleteBodies(context, id + "F61", {"entities" : qUnion([Q0])});
        }
        {
            var Q0;
            Q0=makeQuery(id+"F25.opPattern","COPY",BODY,{"derivedFrom":makeQuery(id+"F15.opPattern","COPY",BODY,{"derivedFrom":makeQuery(id+"F14.opPattern","COPY",BODY,{"derivedFrom":makeQuery(id+"F8.opExtrude","SWEPT_BODY",BODY,{"disambiguationData":[OSD([sQuery(id+"F7.wireOp",EDGE,"E7.0"),sQuery(id+"F7.wireOp",EDGE,"E10"),sQuery(id+"F7.wireOp",EDGE,"E11"),sQuery(id+"F7.wireOp",EDGE,"E12.1.0"),sQuery(id+"F7.wireOp",EDGE,"E12.1.1"),sQuery(id+"F7.wireOp",EDGE,"E12.2.0"),sQuery(id+"F7.wireOp",EDGE,"E12.2.1"),sQuery(id+"F7.wireOp",EDGE,"E12.3.0"),sQuery(id+"F7.wireOp",EDGE,"E12.3.1"),sQuery(id+"F7.wireOp",EDGE,"E12.4.0"),sQuery(id+"F7.wireOp",EDGE,"E12.4.1"),sQuery(id+"F7.wireOp",EDGE,"E12.5.0"),sQuery(id+"F7.wireOp",EDGE,"E12.5.1"),sQuery(id+"F7.wireOp",EDGE,"E12.6.0"),sQuery(id+"F7.wireOp",EDGE,"E13"),sQuery(id+"F7.wireOp",EDGE,"E14")])]}),"instanceName":"1"}),"instanceName":"1"}),"instanceName":"1"});
            deleteBodies(context, id + "F62", {"entities" : qUnion([Q0])});
        }
        {
            var Q0;
            Q0=makeQuery(id+"F25.opPattern","COPY",BODY,{"derivedFrom":makeQuery(id+"F15.opPattern","COPY",BODY,{"derivedFrom":makeQuery(id+"F14.opPattern","COPY",BODY,{"derivedFrom":makeQuery(id+"F8.opExtrude","SWEPT_BODY",BODY,{"disambiguationData":[OSD([sQuery(id+"F7.wireOp",EDGE,"E7.0"),sQuery(id+"F7.wireOp",EDGE,"E10"),sQuery(id+"F7.wireOp",EDGE,"E11"),sQuery(id+"F7.wireOp",EDGE,"E12.1.0"),sQuery(id+"F7.wireOp",EDGE,"E12.1.1"),sQuery(id+"F7.wireOp",EDGE,"E12.2.0"),sQuery(id+"F7.wireOp",EDGE,"E12.2.1"),sQuery(id+"F7.wireOp",EDGE,"E12.3.0"),sQuery(id+"F7.wireOp",EDGE,"E12.3.1"),sQuery(id+"F7.wireOp",EDGE,"E12.4.0"),sQuery(id+"F7.wireOp",EDGE,"E12.4.1"),sQuery(id+"F7.wireOp",EDGE,"E12.5.0"),sQuery(id+"F7.wireOp",EDGE,"E12.5.1"),sQuery(id+"F7.wireOp",EDGE,"E12.6.0"),sQuery(id+"F7.wireOp",EDGE,"E13"),sQuery(id+"F7.wireOp",EDGE,"E14")])]}),"instanceName":"1"}),"instanceName":"1"}),"instanceName":"2"});
            deleteBodies(context, id + "F63", {"entities" : qUnion([Q0])});
        }
    });
